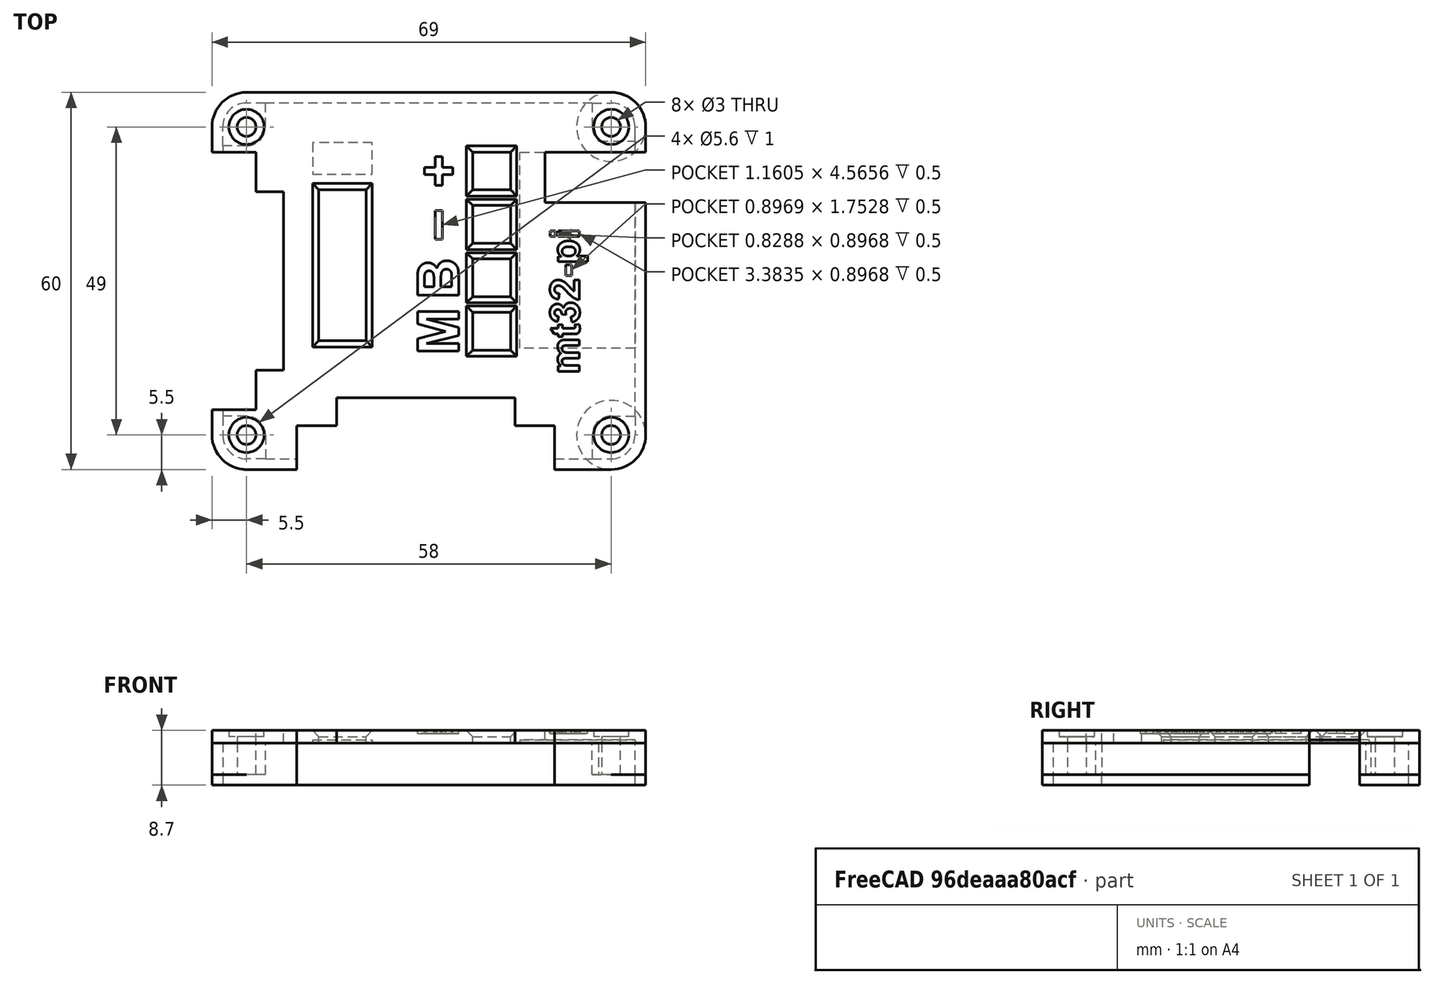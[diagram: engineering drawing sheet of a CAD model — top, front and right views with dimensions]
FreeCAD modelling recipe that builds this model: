
FCSTD DOCUMENT  (FreeCAD 0.21R33668 +26 (Git))
Label: case
License: All rights reserved
LicenseURL: https://en.wikipedia.org/wiki/All_rights_reserved
objects: Sketcher::SketchObject×9, Part::Extrusion×9, Part::Cut×8, Part::Part2DObjectPython×1, Part::Chamfer×1, Part::MultiFuse×1, Mesh::Feature×1
note: 29 computed .brp shape members not serialized (recipe doc carries the construction recipe); baked Part::Feature solids carry a one-line shape summary decoded from their .brp

FEATURE [Sketcher::SketchObject] Sketch001
  FullyConstrained = true
  MapMode = 5
  sketch-geometry (30):
    g0: LineSegment StartX=5.50002 StartY=-5.68372e-08 StartZ=0 EndX=63.5 EndY=-5.68372e-08 EndZ=0
    g1: LineSegment StartX=69 StartY=5.5 StartZ=0 EndX=69 EndY=54.5 EndZ=0
    g2: LineSegment StartX=63.5 StartY=60 StartZ=0 EndX=5.50002 EndY=60 EndZ=0
    g3: LineSegment StartX=8.50002 StartY=1.7 StartZ=0 EndX=60.5 EndY=1.7 EndZ=0
    g4: LineSegment StartX=67.3 StartY=8.5 StartZ=0 EndX=67.3 EndY=51.5 EndZ=0
    g5: LineSegment StartX=60.5 StartY=58.3 StartZ=0 EndX=8.50002 EndY=58.3 EndZ=0
    g6: ArcOfCircle CenterX=63.5 CenterY=54.5 CenterZ=0 NormalX=0 NormalY=0 NormalZ=1 AngleXU=0 Radius=5.5 StartAngle=0 EndAngle=1.5708
    g7: ArcOfCircle CenterX=63.5 CenterY=5.5 CenterZ=0 NormalX=0 NormalY=0 NormalZ=1 AngleXU=0 Radius=5.5 StartAngle=4.71239 EndAngle=6.28319
    g8: ArcOfCircle CenterX=5.50002 CenterY=54.5 CenterZ=0 NormalX=0 NormalY=0 NormalZ=1 AngleXU=0 Radius=5.5 StartAngle=1.5708 EndAngle=3.14159
    g9: Circle CenterX=63.5 CenterY=5.5 CenterZ=0 NormalX=0 NormalY=0 NormalZ=1 AngleXU=0 Radius=1.5
    g10: Circle CenterX=63.5 CenterY=54.5 CenterZ=0 NormalX=0 NormalY=0 NormalZ=1 AngleXU=0 Radius=1.5
    g11: Circle CenterX=5.50002 CenterY=54.5 CenterZ=0 NormalX=0 NormalY=0 NormalZ=1 AngleXU=0 Radius=1.5
    g12: ArcOfCircle CenterX=5.50002 CenterY=54.5 CenterZ=0 NormalX=0 NormalY=0 NormalZ=1 AngleXU=0 Radius=3 StartAngle=4.71239 EndAngle=6.28319
    g13: ArcOfCircle CenterX=63.5 CenterY=54.5 CenterZ=0 NormalX=0 NormalY=0 NormalZ=1 AngleXU=0 Radius=3 StartAngle=3.14159 EndAngle=4.71239
    g14: ArcOfCircle CenterX=63.5 CenterY=5.5 CenterZ=0 NormalX=0 NormalY=0 NormalZ=1 AngleXU=0 Radius=3 StartAngle=1.5708 EndAngle=3.14159
    g15: ArcOfCircle CenterX=5.50002 CenterY=5.5 CenterZ=0 NormalX=0 NormalY=0 NormalZ=1 AngleXU=0 Radius=3 StartAngle=0 EndAngle=1.5708
    g16: LineSegment StartX=8.50002 StartY=54.5 StartZ=0 EndX=8.50002 EndY=58.3 EndZ=0
    g17: LineSegment StartX=5.50002 StartY=51.5 StartZ=0 EndX=1.70002 EndY=51.5 EndZ=0
    g18: LineSegment StartX=1.70002 StartY=51.5 StartZ=0 EndX=1.70002 EndY=8.5 EndZ=0
    g19: LineSegment StartX=5.50002 StartY=8.5 StartZ=0 EndX=1.70002 EndY=8.5 EndZ=0
    g20: LineSegment StartX=8.50002 StartY=5.5 StartZ=0 EndX=8.50002 EndY=1.7 EndZ=0
    g21: Circle CenterX=5.50002 CenterY=5.5 CenterZ=0 NormalX=0 NormalY=0 NormalZ=1 AngleXU=0 Radius=1.5
    g22: LineSegment StartX=63.5 StartY=51.5 StartZ=0 EndX=67.3 EndY=51.5 EndZ=0
    g23: LineSegment StartX=63.5 StartY=8.5 StartZ=0 EndX=67.3 EndY=8.5 EndZ=0
    g24: LineSegment StartX=60.5 StartY=5.5 StartZ=0 EndX=60.5 EndY=1.7 EndZ=0
    g25: LineSegment StartX=60.5 StartY=58.3 StartZ=0 EndX=60.5 EndY=54.5 EndZ=0
    g26: LineSegment StartX=2.09555e-05 StartY=54.5 StartZ=0 EndX=2.09555e-05 EndY=5.5 EndZ=0
    g27: ArcOfCircle CenterX=5.50002 CenterY=5.5 CenterZ=0 NormalX=0 NormalY=0 NormalZ=1 AngleXU=0 Radius=5.5 StartAngle=3.14159 EndAngle=4.71239
    g28: LineSegment StartX=5.50002 StartY=-5.68372e-08 StartZ=0 EndX=0 EndY=0 EndZ=0
    g29: LineSegment StartX=2.09555e-05 StartY=5.5 StartZ=0 EndX=0 EndY=0 EndZ=0
  constraints (72):
    c: Horizontal(g0)
    c: Horizontal(g2)
    c: Vertical(g1)
    c: Horizontal(g3)
    c: Horizontal(g5)
    c: Vertical(g4)
    c: Coincident(g11,g8)
    c: Coincident(g12,g8)
    c: Vertical(g16)
    c: Horizontal(g17)
    c: Tangent(g12,g17) = 1.5708
    c: Tangent(g12,g16) = -1.5708
    c: Coincident(g5,g16)
    c: Coincident(g18,g17)
    c: Vertical(g18)
    c: Horizontal(g19)
    c: Vertical(g20)
    c: Coincident(g18,g19)
    c: Tangent(g15,g19) = -1.5708
    c: Tangent(g15,g20) = 1.5708
    c: Coincident(g3,g20)
    c: Distance(g0,g2) = 60
    c: Horizontal(g22)
    c: Horizontal(g23)
    c: Vertical(g24)
    c: Coincident(g3,g24)
    c: Coincident(g4,g23)
    c: Tangent(g14,g24) = -1.5708
    c: Tangent(g14,g23) = 1.5708
    c: Tangent(g13,g22) = -1.5708
    c: Coincident(g4,g22)
    c: Coincident(g25,g5)
    c: Vertical(g25)
    c: Equal(g11,g10)
    c: Equal(g10,g9)
    c: Equal(g9,g21)
    c: Equal(g13,g12)
    c: Equal(g12,g15)
    c: Equal(g15,g14)
    c: Coincident(g6,g13)
    c: Coincident(g6,g10)
    c: Tangent(g25,g13) = -1.5708
    c: Coincident(g14,g7)
    c: Coincident(g14,g9)
    c: Tangent(g2,g8) = -1.5708
    c: Tangent(g2,g6) = -1.5708
    c: Tangent(g1,g6) = -1.5708
    c: Tangent(g1,g7) = -1.5708
    c: Tangent(g0,g7) = -1.5708
    c: Equal(g16,g19)
    c: Equal(g19,g24)
    c: Equal(g24,g23)
    c: Diameter(g11) = 3
    c: Distance(g5,g2) = 1.7
    c: Radius(g12) = 3
    c: Vertical(g26)
    c: Coincident(g27,g15)
    c: Tangent(g27,g26) = -1.5708
    c: Tangent(g27,g0) = -1.5708
    c: Coincident(g28,g0)
    c: Coincident(g28,g-1)
    c: Tangent(g28,g27)
    c: Coincident(g29,g26)
    c: Coincident(g29,g28)
    c: Tangent(g29,g27)
    c: Tangent(g26,g8) = -1.5708
    c: Equal(g8,g27)
    c: Equal(g27,g7)
    c: Equal(g7,g6)
    c: Coincident(g21,g15)
    c: Distance(g8,g1) = 69
    c: Distance(g8,g26) = 5.5
FEATURE [Part::Extrusion] Extrude
  Base = -> Sketch001
  Dir = (0,0,1)
  DirMode = 2
  FaceMakerClass = Part::FaceMakerBullseye
  LengthFwd = 5
  LengthRev = 0
  Solid = true
  Symmetric = false
FEATURE [Sketcher::SketchObject] Sketch002
  FullyConstrained = true
  MapMode = 5
  expr: Constraints[21] = Sketch001.Constraints[21]
  expr: Constraints[52] = Sketch001.Constraints[52]
  expr: Constraints[53] = Sketch001.Constraints[53]
  expr: Constraints[54] = Sketch001.Constraints[54]
  expr: Constraints[70] = Sketch001.Constraints[70]
  expr: Constraints[71] = Sketch001.Constraints[71]
  sketch-geometry (42):
    g0: LineSegment StartX=5.5 StartY=-9.28724e-08 StartZ=0 EndX=63.5 EndY=-9.28724e-08 EndZ=0
    g1: LineSegment StartX=69 StartY=5.5 StartZ=0 EndX=69 EndY=54.5 EndZ=0
    g2: LineSegment StartX=63.5 StartY=60 StartZ=0 EndX=5.5 EndY=60 EndZ=0
    g3: LineSegment StartX=8.5 StartY=1.7 StartZ=0 EndX=60.5 EndY=1.7 EndZ=0
    g4: LineSegment StartX=67.3 StartY=8.5 StartZ=0 EndX=67.3 EndY=51.5 EndZ=0
    g5: LineSegment StartX=60.5 StartY=58.3 StartZ=0 EndX=8.5 EndY=58.3 EndZ=0
    g6: ArcOfCircle CenterX=63.5 CenterY=54.5 CenterZ=0 NormalX=0 NormalY=0 NormalZ=1 AngleXU=0 Radius=5.5 StartAngle=0 EndAngle=1.5708
    g7: ArcOfCircle CenterX=63.5 CenterY=5.5 CenterZ=0 NormalX=0 NormalY=0 NormalZ=1 AngleXU=0 Radius=5.5 StartAngle=4.71239 EndAngle=6.28319
    g8: ArcOfCircle CenterX=5.5 CenterY=54.5 CenterZ=0 NormalX=0 NormalY=0 NormalZ=1 AngleXU=0 Radius=5.5 StartAngle=1.5708 EndAngle=3.14159
    g9: Circle CenterX=63.5 CenterY=5.5 CenterZ=0 NormalX=0 NormalY=0 NormalZ=1 AngleXU=0 Radius=1.5
    g10: Circle CenterX=63.5 CenterY=54.5 CenterZ=0 NormalX=0 NormalY=0 NormalZ=1 AngleXU=0 Radius=1.5
    g11: Circle CenterX=5.5 CenterY=54.5 CenterZ=0 NormalX=0 NormalY=0 NormalZ=1 AngleXU=0 Radius=1.5
    g12: ArcOfCircle CenterX=5.5 CenterY=54.5 CenterZ=0 NormalX=0 NormalY=0 NormalZ=1 AngleXU=0 Radius=3 StartAngle=4.71239 EndAngle=6.28319
    g13: ArcOfCircle CenterX=63.5 CenterY=54.5 CenterZ=0 NormalX=0 NormalY=0 NormalZ=1 AngleXU=0 Radius=3 StartAngle=3.14159 EndAngle=4.71239
    g14: ArcOfCircle CenterX=63.5 CenterY=5.5 CenterZ=0 NormalX=0 NormalY=0 NormalZ=1 AngleXU=0 Radius=3 StartAngle=1.5708 EndAngle=3.14159
    g15: ArcOfCircle CenterX=5.5 CenterY=5.5 CenterZ=0 NormalX=0 NormalY=0 NormalZ=1 AngleXU=0 Radius=3 StartAngle=0 EndAngle=1.5708
    g16: LineSegment StartX=8.5 StartY=54.5 StartZ=0 EndX=8.5 EndY=58.3 EndZ=0
    g17: LineSegment StartX=5.5 StartY=51.5 StartZ=0 EndX=1.7 EndY=51.5 EndZ=0
    g18: LineSegment StartX=1.7 StartY=51.5 StartZ=0 EndX=1.7 EndY=8.5 EndZ=0
    g19: LineSegment StartX=5.5 StartY=8.5 StartZ=0 EndX=1.7 EndY=8.5 EndZ=0
    g20: LineSegment StartX=8.5 StartY=5.5 StartZ=0 EndX=8.5 EndY=1.7 EndZ=0
    g21: Circle CenterX=5.5 CenterY=5.5 CenterZ=0 NormalX=0 NormalY=0 NormalZ=1 AngleXU=0 Radius=1.5
    g22: LineSegment StartX=63.5 StartY=51.5 StartZ=0 EndX=67.3 EndY=51.5 EndZ=0
    g23: LineSegment StartX=63.5 StartY=8.5 StartZ=0 EndX=67.3 EndY=8.5 EndZ=0
    g24: LineSegment StartX=60.5 StartY=5.5 StartZ=0 EndX=60.5 EndY=1.7 EndZ=0
    g25: LineSegment StartX=60.5 StartY=58.3 StartZ=0 EndX=60.5 EndY=54.5 EndZ=0
    g26: LineSegment StartX=2.40654e-07 StartY=54.5 StartZ=0 EndX=2.40654e-07 EndY=5.5 EndZ=0
    g27: ArcOfCircle CenterX=5.5 CenterY=5.5 CenterZ=0 NormalX=0 NormalY=0 NormalZ=1 AngleXU=0 Radius=5.5 StartAngle=3.14159 EndAngle=4.71239
    g28: LineSegment StartX=5.5 StartY=-9.28724e-08 StartZ=0 EndX=0 EndY=0 EndZ=0
    g29: LineSegment StartX=2.40654e-07 StartY=5.5 StartZ=0 EndX=0 EndY=0 EndZ=0
    g30: LineSegment StartX=1.7 StartY=51.5 StartZ=0 EndX=1.7 EndY=54.5 EndZ=0
    g31: LineSegment StartX=8.5 StartY=58.3 StartZ=0 EndX=5.5 EndY=58.3 EndZ=0
    g32: ArcOfCircle CenterX=5.5 CenterY=54.5 CenterZ=0 NormalX=0 NormalY=0 NormalZ=1 AngleXU=0 Radius=3.8 StartAngle=1.5708 EndAngle=3.14159
    g33: LineSegment StartX=60.5 StartY=58.3 StartZ=0 EndX=63.5 EndY=58.3 EndZ=0
    g34: LineSegment StartX=67.3 StartY=51.5 StartZ=0 EndX=67.3 EndY=54.5 EndZ=0
    g35: LineSegment StartX=67.3 StartY=8.5 StartZ=0 EndX=67.3 EndY=5.5 EndZ=0
    g36: LineSegment StartX=60.5 StartY=1.7 StartZ=0 EndX=63.5 EndY=1.7 EndZ=0
    g37: LineSegment StartX=8.5 StartY=1.7 StartZ=0 EndX=5.5 EndY=1.7 EndZ=0
    g38: LineSegment StartX=1.7 StartY=8.5 StartZ=0 EndX=1.7 EndY=5.5 EndZ=0
    g39: ArcOfCircle CenterX=5.5 CenterY=5.5 CenterZ=0 NormalX=0 NormalY=0 NormalZ=1 AngleXU=0 Radius=3.8 StartAngle=3.14159 EndAngle=4.71239
    g40: ArcOfCircle CenterX=63.5 CenterY=5.5 CenterZ=0 NormalX=0 NormalY=0 NormalZ=1 AngleXU=0 Radius=3.8 StartAngle=4.71239 EndAngle=6.28319
    g41: ArcOfCircle CenterX=63.5 CenterY=54.5 CenterZ=0 NormalX=0 NormalY=0 NormalZ=1 AngleXU=0 Radius=3.8 StartAngle=6e-16 EndAngle=1.5708
  constraints (100):
    c: Horizontal(g0)
    c: Horizontal(g2)
    c: Vertical(g1)
    c: Horizontal(g3)
    c: Horizontal(g5)
    c: Vertical(g4)
    c: Coincident(g11,g8)
    c: Coincident(g12,g8)
    c: Vertical(g16)
    c: Horizontal(g17)
    c: Tangent(g12,g17) = 1.5708
    c: Tangent(g12,g16) = -1.5708
    c: Coincident(g5,g16)
    c: Coincident(g18,g17)
    c: Vertical(g18)
    c: Horizontal(g19)
    c: Vertical(g20)
    c: Coincident(g18,g19)
    c: Tangent(g15,g19) = -1.5708
    c: Tangent(g15,g20) = 1.5708
    c: Coincident(g3,g20)
    c: Distance(g0,g2) = 60
    c: Horizontal(g22)
    c: Horizontal(g23)
    c: Vertical(g24)
    c: Coincident(g3,g24)
    c: Coincident(g4,g23)
    c: Tangent(g14,g24) = -1.5708
    c: Tangent(g14,g23) = 1.5708
    c: Tangent(g13,g22) = -1.5708
    c: Coincident(g4,g22)
    c: Coincident(g25,g5)
    c: Vertical(g25)
    c: Equal(g11,g10)
    c: Equal(g10,g9)
    c: Equal(g9,g21)
    c: Equal(g13,g12)
    c: Equal(g12,g15)
    c: Equal(g15,g14)
    c: Coincident(g6,g13)
    c: Coincident(g6,g10)
    c: Tangent(g25,g13) = -1.5708
    c: Coincident(g14,g7)
    c: Coincident(g14,g9)
    c: Tangent(g2,g8) = -1.5708
    c: Tangent(g2,g6) = -1.5708
    c: Tangent(g1,g6) = -1.5708
    c: Tangent(g1,g7) = -1.5708
    c: Tangent(g0,g7) = -1.5708
    c: Equal(g16,g19)
    c: Equal(g19,g24)
    c: Equal(g24,g23)
    c: Diameter(g11) = 3
    c: Distance(g5,g2) = 1.7
    c: Radius(g12) = 3
    c: Vertical(g26)
    c: Coincident(g27,g15)
    c: Tangent(g27,g26) = -1.5708
    c: Tangent(g27,g0) = -1.5708
    c: Coincident(g28,g0)
    c: Coincident(g28,g-1)
    c: Tangent(g28,g27)
    c: Coincident(g29,g26)
    c: Coincident(g29,g28)
    c: Tangent(g29,g27)
    c: Tangent(g26,g8) = -1.5708
    c: Equal(g8,g27)
    c: Equal(g27,g7)
    c: Equal(g7,g6)
    c: Coincident(g21,g15)
    c: Distance(g8,g1) = 69
    c: Distance(g8,g26) = 5.5
    c: Coincident(g30,g17)
    c: Vertical(g30)
    c: Coincident(g31,g5)
    c: Horizontal(g31)
    c: Coincident(g32,g8)
    c: Coincident(g32,g31)
    c: Tangent(g32,g30) = 1.5708
    c: Coincident(g33,g5)
    c: Horizontal(g33)
    c: Coincident(g34,g4)
    c: Vertical(g34)
    c: Coincident(g35,g4)
    c: Vertical(g35)
    c: Coincident(g36,g3)
    c: Horizontal(g36)
    c: Coincident(g37,g3)
    c: Horizontal(g37)
    c: Coincident(g38,g18)
    c: Vertical(g38)
    c: Coincident(g39,g15)
    c: Coincident(g39,g38)
    c: Coincident(g40,g7)
    c: Coincident(g40,g36)
    c: Coincident(g41,g6)
    c: Coincident(g41,g33)
    c: Tangent(g41,g34) = -1.5708
    c: Tangent(g40,g35) = 1.5708
    c: Tangent(g39,g37) = 1.5708
FEATURE [Sketcher::SketchObject] Sketch003
  FullyConstrained = true
  MapMode = 5
  Placement = pos=(0,0,5) rot=(0,0,1;0rad)
  Support = -> [Extrude]
  expr: Constraints[109] = Sketch001.Constraints[21]
  expr: Constraints[140] = Sketch001.Constraints[52]
  expr: Constraints[141] = Sketch001.Constraints[53]
  expr: Constraints[142] = Sketch001.Constraints[54]
  expr: Constraints[158] = Sketch001.Constraints[70]
  expr: Constraints[159] = Sketch001.Constraints[71]
  sketch-geometry (64):
    g0: LineSegment StartX=17 StartY=44.5 StartZ=0 EndX=24.5 EndY=44.5 EndZ=0
    g1: LineSegment StartX=24.5 StartY=44.5 StartZ=0 EndX=24.5 EndY=20.5 EndZ=0
    g2: LineSegment StartX=24.5 StartY=20.5 StartZ=0 EndX=17 EndY=20.5 EndZ=0
    g3: LineSegment StartX=17 StartY=20.5 StartZ=0 EndX=17 EndY=44.5 EndZ=0
    g4: LineSegment StartX=41.5 StartY=50.5 StartZ=0 EndX=47.5 EndY=50.5 EndZ=0
    g5: LineSegment StartX=47.5 StartY=50.5 StartZ=0 EndX=47.5 EndY=44.5 EndZ=0
    g6: LineSegment StartX=47.5 StartY=44.5 StartZ=0 EndX=41.5 EndY=44.5 EndZ=0
    g7: LineSegment StartX=41.5 StartY=44.5 StartZ=0 EndX=41.5 EndY=50.5 EndZ=0
    g8: LineSegment StartX=41.5 StartY=42 StartZ=0 EndX=47.5 EndY=42 EndZ=0
    g9: LineSegment StartX=47.5 StartY=42 StartZ=0 EndX=47.5 EndY=36 EndZ=0
    g10: LineSegment StartX=47.5 StartY=36 StartZ=0 EndX=41.5 EndY=36 EndZ=0
    g11: LineSegment StartX=41.5 StartY=36 StartZ=0 EndX=41.5 EndY=42 EndZ=0
    g12: LineSegment StartX=41.5 StartY=33.5 StartZ=0 EndX=47.5 EndY=33.5 EndZ=0
    g13: LineSegment StartX=47.5 StartY=33.5 StartZ=0 EndX=47.5 EndY=27.5 EndZ=0
    g14: LineSegment StartX=47.5 StartY=27.5 StartZ=0 EndX=41.5 EndY=27.5 EndZ=0
    g15: LineSegment StartX=41.5 StartY=27.5 StartZ=0 EndX=41.5 EndY=33.5 EndZ=0
    g16: LineSegment StartX=41.5 StartY=25 StartZ=0 EndX=47.5 EndY=25 EndZ=0
    g17: LineSegment StartX=47.5 StartY=25 StartZ=0 EndX=47.5 EndY=19 EndZ=0
    g18: LineSegment StartX=47.5 StartY=19 StartZ=0 EndX=41.5 EndY=19 EndZ=0
    g19: LineSegment StartX=41.5 StartY=19 StartZ=0 EndX=41.5 EndY=25 EndZ=0
    g20: LineSegment StartX=41.5 StartY=44.5 StartZ=0 EndX=41.5 EndY=42 EndZ=0
    g21: LineSegment StartX=41.5 StartY=36 StartZ=0 EndX=41.5 EndY=33.5 EndZ=0
    g22: LineSegment StartX=41.5 StartY=27.5 StartZ=0 EndX=41.5 EndY=25 EndZ=0
    g23: LineSegment StartX=47.5 StartY=25 StartZ=0 EndX=47.5 EndY=27.5 EndZ=0
    g24: LineSegment StartX=47.5 StartY=33.5 StartZ=0 EndX=47.5 EndY=36 EndZ=0
    g25: LineSegment StartX=47.5 StartY=42 StartZ=0 EndX=47.5 EndY=44.5 EndZ=0
    g26: LineSegment StartX=61.73 StartY=18.27 StartZ=0 EndX=65.28 EndY=18.27 EndZ=0
    g27: LineSegment StartX=65.28 StartY=18.27 StartZ=0 EndX=65.28 EndY=9.62 EndZ=0
    g28: LineSegment StartX=65.28 StartY=9.62 StartZ=0 EndX=61.73 EndY=9.62 EndZ=0
    g29: LineSegment StartX=61.73 StartY=9.62 StartZ=0 EndX=61.73 EndY=18.27 EndZ=0
    g30: LineSegment StartX=55.5 StartY=11.85 StartZ=0 EndX=59.05 EndY=11.85 EndZ=0
    g31: LineSegment StartX=59.05 StartY=11.85 StartZ=0 EndX=59.05 EndY=3.2 EndZ=0
    g32: LineSegment StartX=59.05 StartY=3.2 StartZ=0 EndX=55.5 EndY=3.2 EndZ=0
    g33: LineSegment StartX=55.5 StartY=3.2 StartZ=0 EndX=55.5 EndY=11.85 EndZ=0
    g34: LineSegment StartX=5.5 StartY=2.71047e-06 StartZ=0 EndX=63.5 EndY=2.71047e-06 EndZ=0
    g35: LineSegment StartX=69 StartY=5.5 StartZ=0 EndX=69 EndY=54.5 EndZ=0
    g36: LineSegment StartX=63.5 StartY=60 StartZ=0 EndX=5.5 EndY=60 EndZ=0
    g37: LineSegment StartX=8.5 StartY=1.7 StartZ=0 EndX=60.5 EndY=1.7 EndZ=0
    g38: LineSegment StartX=67.3 StartY=8.5 StartZ=0 EndX=67.3 EndY=51.5 EndZ=0
    g39: LineSegment StartX=60.5 StartY=58.3 StartZ=0 EndX=8.5 EndY=58.3 EndZ=0
    g40: ArcOfCircle CenterX=63.5 CenterY=54.5 CenterZ=0 NormalX=0 NormalY=0 NormalZ=1 AngleXU=0 Radius=5.5 StartAngle=4e-16 EndAngle=1.5708
    g41: ArcOfCircle CenterX=63.5 CenterY=5.5 CenterZ=0 NormalX=0 NormalY=0 NormalZ=1 AngleXU=0 Radius=5.5 StartAngle=4.71239 EndAngle=6.28319
    g42: ArcOfCircle CenterX=5.5 CenterY=54.5 CenterZ=0 NormalX=0 NormalY=0 NormalZ=1 AngleXU=0 Radius=5.5 StartAngle=1.5708 EndAngle=3.14159
    g43: Circle CenterX=63.5 CenterY=5.5 CenterZ=0 NormalX=0 NormalY=0 NormalZ=1 AngleXU=0 Radius=1.5
    g44: Circle CenterX=63.5 CenterY=54.5 CenterZ=0 NormalX=0 NormalY=0 NormalZ=1 AngleXU=0 Radius=1.5
    g45: Circle CenterX=5.5 CenterY=54.5 CenterZ=0 NormalX=0 NormalY=0 NormalZ=1 AngleXU=0 Radius=1.5
    g46: ArcOfCircle CenterX=5.5 CenterY=54.5 CenterZ=0 NormalX=0 NormalY=0 NormalZ=1 AngleXU=0 Radius=3 StartAngle=4.71239 EndAngle=6.28319
    g47: ArcOfCircle CenterX=63.5 CenterY=54.5 CenterZ=0 NormalX=0 NormalY=0 NormalZ=1 AngleXU=0 Radius=3 StartAngle=3.14159 EndAngle=4.71239
    g48: ArcOfCircle CenterX=63.5 CenterY=5.5 CenterZ=0 NormalX=0 NormalY=0 NormalZ=1 AngleXU=0 Radius=3 StartAngle=1.5708 EndAngle=3.14159
    g49: ArcOfCircle CenterX=5.5 CenterY=5.5 CenterZ=0 NormalX=0 NormalY=0 NormalZ=1 AngleXU=0 Radius=3 StartAngle=0 EndAngle=1.5708
    g50: LineSegment StartX=8.5 StartY=54.5 StartZ=0 EndX=8.5 EndY=58.3 EndZ=0
    g51: LineSegment StartX=5.5 StartY=51.5 StartZ=0 EndX=1.7 EndY=51.5 EndZ=0
    g52: LineSegment StartX=1.7 StartY=51.5 StartZ=0 EndX=1.7 EndY=8.5 EndZ=0
    g53: LineSegment StartX=5.5 StartY=8.5 StartZ=0 EndX=1.7 EndY=8.5 EndZ=0
    g54: LineSegment StartX=8.5 StartY=5.5 StartZ=0 EndX=8.5 EndY=1.7 EndZ=0
    g55: Circle CenterX=5.5 CenterY=5.5 CenterZ=0 NormalX=0 NormalY=0 NormalZ=1 AngleXU=0 Radius=1.5
    g56: LineSegment StartX=63.5 StartY=51.5 StartZ=0 EndX=67.3 EndY=51.5 EndZ=0
    g57: LineSegment StartX=63.5 StartY=8.5 StartZ=0 EndX=67.3 EndY=8.5 EndZ=0
    g58: LineSegment StartX=60.5 StartY=5.5 StartZ=0 EndX=60.5 EndY=1.7 EndZ=0
    g59: LineSegment StartX=60.5 StartY=58.3 StartZ=0 EndX=60.5 EndY=54.5 EndZ=0
    g60: LineSegment StartX=2.53122e-07 StartY=54.5 StartZ=0 EndX=2.53122e-07 EndY=5.5 EndZ=0
    g61: ArcOfCircle CenterX=5.5 CenterY=5.5 CenterZ=0 NormalX=0 NormalY=0 NormalZ=1 AngleXU=0 Radius=5.5 StartAngle=3.14159 EndAngle=4.71239
    g62: LineSegment StartX=5.5 StartY=2.71047e-06 StartZ=0 EndX=0 EndY=0 EndZ=0
    g63: LineSegment StartX=2.53122e-07 StartY=5.5 StartZ=0 EndX=0 EndY=0 EndZ=0
  constraints (168):
    c: Coincident(g0,g1)
    c: Coincident(g1,g2)
    c: Coincident(g2,g3)
    c: Coincident(g3,g0)
    c: Horizontal(g0)
    c: Horizontal(g2)
    c: Vertical(g1)
    c: Vertical(g3)
    c: Coincident(g4,g5)
    c: Coincident(g5,g6)
    c: Coincident(g6,g7)
    c: Coincident(g7,g4)
    c: Horizontal(g4)
    c: Horizontal(g6)
    c: Vertical(g5)
    c: Vertical(g7)
    c: Coincident(g8,g9)
    c: Coincident(g9,g10)
    c: Coincident(g10,g11)
    c: Coincident(g11,g8)
    c: Horizontal(g8)
    c: Horizontal(g10)
    c: Vertical(g9)
    c: Vertical(g11)
    c: Coincident(g12,g13)
    c: Coincident(g13,g14)
    c: Coincident(g14,g15)
    c: Coincident(g15,g12)
    c: Horizontal(g12)
    c: Horizontal(g14)
    c: Vertical(g13)
    c: Vertical(g15)
    c: Coincident(g16,g17)
    c: Coincident(g17,g18)
    c: Coincident(g18,g19)
    c: Coincident(g19,g16)
    c: Horizontal(g16)
    c: Horizontal(g18)
    c: Vertical(g17)
    c: Vertical(g19)
    c: Coincident(g20,g6)
    c: Coincident(g20,g8)
    c: Coincident(g21,g10)
    c: Coincident(g21,g12)
    c: Coincident(g22,g14)
    c: Coincident(g22,g16)
    c: Coincident(g23,g16)
    c: Coincident(g23,g13)
    c: Coincident(g24,g12)
    c: Coincident(g24,g9)
    c: Coincident(g25,g8)
    c: Coincident(g25,g5)
    c: Vertical(g20)
    c: Vertical(g25)
    c: Vertical(g21)
    c: Vertical(g24)
    c: Vertical(g23)
    c: Vertical(g22)
    c: Equal(g15,g11)
    c: Equal(g11,g7)
    c: Equal(g7,g19)
    c: Equal(g20,g21)
    c: Equal(g21,g22)
    c: Distance(g4) = 6
    c: Distance(g5) = 6
    c: DistanceY(g8,g4) = 8.5
    c: Distance(g3) = 24
    c: Distance(g0) = 7.5
    c: Coincident(g26,g27)
    c: Coincident(g27,g28)
    c: Coincident(g28,g29)
    c: Coincident(g29,g26)
    c: Horizontal(g26)
    c: Horizontal(g28)
    c: Vertical(g27)
    c: Vertical(g29)
    c: Coincident(g30,g31)
    c: Coincident(g31,g32)
    c: Coincident(g32,g33)
    c: Coincident(g33,g30)
    c: Horizontal(g30)
    c: Horizontal(g32)
    c: Vertical(g31)
    c: Vertical(g33)
    c: Equal(g33,g29)
    c: Equal(g30,g26)
    c: Distance(g33) = 8.65
    c: Distance(g30) = 3.55
    c: Horizontal(g34)
    c: Horizontal(g36)
    c: Vertical(g35)
    c: Horizontal(g37)
    c: Horizontal(g39)
    c: Vertical(g38)
    c: Coincident(g45,g42)
    c: Coincident(g46,g42)
    c: Vertical(g50)
    c: Horizontal(g51)
    c: Tangent(g46,g51) = 1.5708
    c: Tangent(g46,g50) = -1.5708
    c: Coincident(g39,g50)
    c: Coincident(g52,g51)
    c: Vertical(g52)
    c: Horizontal(g53)
    c: Vertical(g54)
    c: Coincident(g52,g53)
    c: Tangent(g49,g53) = -1.5708
    c: Tangent(g49,g54) = 1.5708
    c: Coincident(g37,g54)
    c: Distance(g34,g36) = 60
    c: Horizontal(g56)
    c: Horizontal(g57)
    c: Vertical(g58)
    c: Coincident(g37,g58)
    c: Coincident(g38,g57)
    c: Tangent(g48,g58) = -1.5708
    c: Tangent(g48,g57) = 1.5708
    c: Tangent(g47,g56) = -1.5708
    c: Coincident(g38,g56)
    c: Coincident(g59,g39)
    c: Vertical(g59)
    c: Equal(g45,g44)
    c: Equal(g44,g43)
    c: Equal(g43,g55)
    c: Equal(g47,g46)
    c: Equal(g46,g49)
    c: Equal(g49,g48)
    c: Coincident(g40,g47)
    c: Coincident(g40,g44)
    c: Tangent(g59,g47) = -1.5708
    c: Coincident(g48,g41)
    c: Coincident(g48,g43)
    c: Tangent(g36,g42) = -1.5708
    c: Tangent(g36,g40) = -1.5708
    c: Tangent(g35,g40) = -1.5708
    c: Tangent(g35,g41) = -1.5708
    c: Tangent(g34,g41) = -1.5708
    c: Equal(g50,g53)
    c: Equal(g53,g58)
    c: Equal(g58,g57)
    c: Diameter(g45) = 3
    c: Distance(g39,g36) = 1.7
    c: Radius(g46) = 3
    c: Vertical(g60)
    c: Coincident(g61,g49)
    c: Tangent(g61,g60) = -1.5708
    c: Tangent(g61,g34) = -1.5708
    c: Coincident(g62,g34)
    c: Coincident(g62,g-1)
    c: Tangent(g62,g61)
    c: Coincident(g63,g60)
    c: Coincident(g63,g62)
    c: Tangent(g63,g61)
    c: Tangent(g60,g42) = -1.5708
    c: Equal(g42,g61)
    c: Equal(g61,g41)
    c: Equal(g41,g40)
    c: Coincident(g55,g49)
    c: Distance(g42,g35) = 69
    c: Distance(g42,g60) = 5.5
    c: Distance(g4,g36) = 9.5
    c: Distance(g4,g35) = 21.5
    c: Distance(g42,g3) = 11.5
    c: Distance(g42,g0) = 10
    c: Distance(g41,g31) = 4.45
    c: Distance(g41,g32) = 2.3
    c: Distance(g41,g27) = 1.78
    c: Distance(g41,g28) = 4.12
FEATURE [Part::Extrusion] Extrude001
  Base = -> Sketch002
  Dir = (0,0,1)
  DirMode = 2
  FaceMakerClass = Part::FaceMakerBullseye
  LengthFwd = 0
  LengthRev = 1.7
  Solid = true
  Symmetric = false
FEATURE [Part::Extrusion] Extrude002
  Base = -> Sketch003
  Dir = (0,0,1)
  DirMode = 2
  FaceMakerClass = Part::FaceMakerBullseye
  LengthFwd = 2
  LengthRev = 0
  Solid = true
  Symmetric = false
FEATURE [Sketcher::SketchObject] Sketch
  FullyConstrained = true
  MapMode = 2
  Support = -> [Sketch001]
  sketch-geometry (24):
    g0: LineSegment StartX=0 StartY=0 StartZ=0 EndX=69 EndY=0 EndZ=0
    g1: LineSegment StartX=69 StartY=0 StartZ=0 EndX=69 EndY=60 EndZ=0
    g2: LineSegment StartX=69 StartY=60 StartZ=0 EndX=0 EndY=60 EndZ=0
    g3: LineSegment StartX=0 StartY=60 StartZ=0 EndX=0 EndY=0 EndZ=0
    g4: LineSegment StartX=0 StartY=9.5 StartZ=0 EndX=0 EndY=50.5 EndZ=0
    g5: LineSegment StartX=13.5 StartY=0 StartZ=0 EndX=54.5 EndY=0 EndZ=0
    g6: LineSegment StartX=54.5 StartY=0 StartZ=0 EndX=54.5 EndY=7 EndZ=0
    g7: LineSegment StartX=48.2 StartY=11.4 StartZ=0 EndX=19.8 EndY=11.4 EndZ=0
    g8: LineSegment StartX=71 StartY=50.5 StartZ=0 EndX=53 EndY=50.5 EndZ=0
    g9: LineSegment StartX=53 StartY=50.5 StartZ=0 EndX=53 EndY=42.5 EndZ=0
    g10: LineSegment StartX=53 StartY=42.5 StartZ=0 EndX=71 EndY=42.5 EndZ=0
    g11: LineSegment StartX=7 StartY=9.5 StartZ=0 EndX=7 EndY=15.8 EndZ=0
    g12: LineSegment StartX=7 StartY=15.8 StartZ=0 EndX=11.4 EndY=15.8 EndZ=0
    g13: LineSegment StartX=7 StartY=9.5 StartZ=0 EndX=0 EndY=9.5 EndZ=0
    g14: LineSegment StartX=0 StartY=50.5 StartZ=0 EndX=7 EndY=50.5 EndZ=0
    g15: LineSegment StartX=7 StartY=50.5 StartZ=0 EndX=7 EndY=44.2 EndZ=0
    g16: LineSegment StartX=7 StartY=44.2 StartZ=0 EndX=11.4 EndY=44.2 EndZ=0
    g17: LineSegment StartX=11.4 StartY=44.2 StartZ=0 EndX=11.4 EndY=15.8 EndZ=0
    g18: LineSegment StartX=13.5 StartY=7 StartZ=0 EndX=19.8 EndY=7 EndZ=0
    g19: LineSegment StartX=19.8 StartY=11.4 StartZ=0 EndX=19.8 EndY=7 EndZ=0
    g20: LineSegment StartX=48.2 StartY=11.4 StartZ=0 EndX=48.2 EndY=7 EndZ=0
    g21: LineSegment StartX=54.5 StartY=7 StartZ=0 EndX=48.2 EndY=7 EndZ=0
    g22: LineSegment StartX=71 StartY=50.5 StartZ=0 EndX=71 EndY=42.5 EndZ=0
    g23: LineSegment StartX=13.5 StartY=7 StartZ=0 EndX=13.5 EndY=0 EndZ=0
  constraints (71):
    c: Coincident(g0,g1)
    c: Coincident(g1,g2)
    c: Coincident(g2,g3)
    c: Coincident(g3,g0)
    c: Horizontal(g0)
    c: Horizontal(g2)
    c: Vertical(g1)
    c: Vertical(g3)
    c: Coincident(g0,g-1)
    c: Distance(g2) = 69
    c: Distance(g1) = 60
    c: Vertical(g4)
    c: PointOnObject(g4,g3)
    c: Coincident(g5,g6)
    c: Horizontal(g5)
    c: Horizontal(g7)
    c: Vertical(g6)
    c: PointOnObject(g5,g0)
    c: Coincident(g8,g9)
    c: Coincident(g9,g10)
    c: Horizontal(g8)
    c: Horizontal(g10)
    c: Vertical(g9)
    c: Distance(g8,g2) = 9.5
    c: Distance(g8,g1) = 16
    c: Distance(g5,g3) = 13.5
    c: Vertical(g11)
    c: Coincident(g12,g11)
    c: Horizontal(g12)
    c: Coincident(g13,g11)
    c: Coincident(g13,g4)
    c: Horizontal(g13)
    c: Distance(g11,g0) = 9.5
    c: Distance(g12,g4) = 11.4
    c: Distance(g4,g2) = 9.5
    c: Coincident(g14,g4)
    c: Horizontal(g14)
    c: Coincident(g15,g14)
    c: Vertical(g15)
    c: Coincident(g16,g15)
    c: Horizontal(g16)
    c: Coincident(g17,g16)
    c: Coincident(g17,g12)
    c: Vertical(g17)
    c: Distance(g15,g4) = 7
    c: Distance(g15,g14) = 6.3
    c: Horizontal(g18)
    c: Coincident(g19,g18)
    c: Vertical(g19)
    c: Vertical(g20)
    c: Coincident(g21,g20)
    c: Horizontal(g21)
    c: Coincident(g7,g19)
    c: Coincident(g7,g20)
    c: Coincident(g6,g21)
    c: Coincident(g22,g8)
    c: Coincident(g22,g10)
    c: Vertical(g22)
    c: Distance(g8,g1) = 2
    c: Distance(g8,g10) = 8
    c: Equal(g15,g11)
    c: Equal(g11,g18)
    c: Equal(g18,g21)
    c: Coincident(g23,g18)
    c: Coincident(g23,g5)
    c: Vertical(g23)
    c: Equal(g12,g16)
    c: Equal(g16,g19)
    c: Equal(g19,g20)
    c: Equal(g6,g13)
    c: Equal(g5,g4)
FEATURE [Part::Extrusion] Extrude003
  Base = -> Sketch
  Dir = (0,0,1)
  DirMode = 2
  FaceMakerClass = Part::FaceMakerBullseye
  LengthFwd = 20
  LengthRev = 20
  Solid = true
  Symmetric = false
FEATURE [Part::Cut] Cut
  Base = -> Extrude
  Tool = -> Extrude003
FEATURE [Part::Cut] Cut001
  Base = -> Extrude001
  Tool = -> Extrude003
FEATURE [Part::Cut] Cut002
  Base = -> Extrude002
  Tool = -> Extrude003
FEATURE [Sketcher::SketchObject] Sketch004
  FullyConstrained = true
  MapMode = 5
  expr: Constraints[21] = Sketch001.Constraints[21]
  expr: Constraints[52] = Sketch001.Constraints[52]
  expr: Constraints[53] = Sketch001.Constraints[53]
  expr: Constraints[54] = Sketch001.Constraints[54]
  expr: Constraints[70] = Sketch001.Constraints[70]
  expr: Constraints[71] = Sketch001.Constraints[71]
  sketch-geometry (30):
    g0: LineSegment StartX=5.50002 StartY=-5.68372e-08 StartZ=0 EndX=63.5 EndY=-5.68372e-08 EndZ=0
    g1: LineSegment StartX=69 StartY=5.5 StartZ=0 EndX=69 EndY=54.5 EndZ=0
    g2: LineSegment StartX=63.5 StartY=60 StartZ=0 EndX=5.50002 EndY=60 EndZ=0
    g3: LineSegment StartX=8.50002 StartY=1.7 StartZ=0 EndX=60.5 EndY=1.7 EndZ=0
    g4: LineSegment StartX=67.3 StartY=8.5 StartZ=0 EndX=67.3 EndY=51.5 EndZ=0
    g5: LineSegment StartX=60.5 StartY=58.3 StartZ=0 EndX=8.50002 EndY=58.3 EndZ=0
    g6: ArcOfCircle CenterX=63.5 CenterY=54.5 CenterZ=0 NormalX=0 NormalY=0 NormalZ=1 AngleXU=0 Radius=5.5 StartAngle=0 EndAngle=1.5708
    g7: ArcOfCircle CenterX=63.5 CenterY=5.5 CenterZ=0 NormalX=0 NormalY=0 NormalZ=1 AngleXU=0 Radius=5.5 StartAngle=4.71239 EndAngle=6.28319
    g8: ArcOfCircle CenterX=5.50002 CenterY=54.5 CenterZ=0 NormalX=0 NormalY=0 NormalZ=1 AngleXU=0 Radius=5.5 StartAngle=1.5708 EndAngle=3.14159
    g9: Circle CenterX=63.5 CenterY=5.5 CenterZ=0 NormalX=0 NormalY=0 NormalZ=1 AngleXU=0 Radius=1.5
    g10: Circle CenterX=63.5 CenterY=54.5 CenterZ=0 NormalX=0 NormalY=0 NormalZ=1 AngleXU=0 Radius=1.5
    g11: Circle CenterX=5.50002 CenterY=54.5 CenterZ=0 NormalX=0 NormalY=0 NormalZ=1 AngleXU=0 Radius=1.5
    g12: ArcOfCircle CenterX=5.50002 CenterY=54.5 CenterZ=0 NormalX=0 NormalY=0 NormalZ=1 AngleXU=0 Radius=3 StartAngle=4.71239 EndAngle=6.28319
    g13: ArcOfCircle CenterX=63.5 CenterY=54.5 CenterZ=0 NormalX=0 NormalY=0 NormalZ=1 AngleXU=0 Radius=3 StartAngle=3.14159 EndAngle=4.71239
    g14: ArcOfCircle CenterX=63.5 CenterY=5.5 CenterZ=0 NormalX=0 NormalY=0 NormalZ=1 AngleXU=0 Radius=3 StartAngle=1.5708 EndAngle=3.14159
    g15: ArcOfCircle CenterX=5.50002 CenterY=5.5 CenterZ=0 NormalX=0 NormalY=0 NormalZ=1 AngleXU=0 Radius=3 StartAngle=0 EndAngle=1.5708
    g16: LineSegment StartX=8.50002 StartY=54.5 StartZ=0 EndX=8.50002 EndY=58.3 EndZ=0
    g17: LineSegment StartX=5.50002 StartY=51.5 StartZ=0 EndX=1.70002 EndY=51.5 EndZ=0
    g18: LineSegment StartX=1.70002 StartY=51.5 StartZ=0 EndX=1.70002 EndY=8.5 EndZ=0
    g19: LineSegment StartX=5.50002 StartY=8.5 StartZ=0 EndX=1.70002 EndY=8.5 EndZ=0
    g20: LineSegment StartX=8.50002 StartY=5.5 StartZ=0 EndX=8.50002 EndY=1.7 EndZ=0
    g21: Circle CenterX=5.50002 CenterY=5.5 CenterZ=0 NormalX=0 NormalY=0 NormalZ=1 AngleXU=0 Radius=1.5
    g22: LineSegment StartX=63.5 StartY=51.5 StartZ=0 EndX=67.3 EndY=51.5 EndZ=0
    g23: LineSegment StartX=63.5 StartY=8.5 StartZ=0 EndX=67.3 EndY=8.5 EndZ=0
    g24: LineSegment StartX=60.5 StartY=5.5 StartZ=0 EndX=60.5 EndY=1.7 EndZ=0
    g25: LineSegment StartX=60.5 StartY=58.3 StartZ=0 EndX=60.5 EndY=54.5 EndZ=0
    g26: LineSegment StartX=2.09555e-05 StartY=54.5 StartZ=0 EndX=2.09555e-05 EndY=5.5 EndZ=0
    g27: ArcOfCircle CenterX=5.50002 CenterY=5.5 CenterZ=0 NormalX=0 NormalY=0 NormalZ=1 AngleXU=0 Radius=5.5 StartAngle=3.14159 EndAngle=4.71239
    g28: LineSegment StartX=5.50002 StartY=-5.68372e-08 StartZ=0 EndX=0 EndY=0 EndZ=0
    g29: LineSegment StartX=2.09555e-05 StartY=5.5 StartZ=0 EndX=0 EndY=0 EndZ=0
  constraints (72):
    c: Horizontal(g0)
    c: Horizontal(g2)
    c: Vertical(g1)
    c: Horizontal(g3)
    c: Horizontal(g5)
    c: Vertical(g4)
    c: Coincident(g11,g8)
    c: Coincident(g12,g8)
    c: Vertical(g16)
    c: Horizontal(g17)
    c: Tangent(g12,g17) = 1.5708
    c: Tangent(g12,g16) = -1.5708
    c: Coincident(g5,g16)
    c: Coincident(g18,g17)
    c: Vertical(g18)
    c: Horizontal(g19)
    c: Vertical(g20)
    c: Coincident(g18,g19)
    c: Tangent(g15,g19) = -1.5708
    c: Tangent(g15,g20) = 1.5708
    c: Coincident(g3,g20)
    c: Distance(g0,g2) = 60
    c: Horizontal(g22)
    c: Horizontal(g23)
    c: Vertical(g24)
    c: Coincident(g3,g24)
    c: Coincident(g4,g23)
    c: Tangent(g14,g24) = -1.5708
    c: Tangent(g14,g23) = 1.5708
    c: Tangent(g13,g22) = -1.5708
    c: Coincident(g4,g22)
    c: Coincident(g25,g5)
    c: Vertical(g25)
    c: Equal(g11,g10)
    c: Equal(g10,g9)
    c: Equal(g9,g21)
    c: Equal(g13,g12)
    c: Equal(g12,g15)
    c: Equal(g15,g14)
    c: Coincident(g6,g13)
    c: Coincident(g6,g10)
    c: Tangent(g25,g13) = -1.5708
    c: Coincident(g14,g7)
    c: Coincident(g14,g9)
    c: Tangent(g2,g8) = -1.5708
    c: Tangent(g2,g6) = -1.5708
    c: Tangent(g1,g6) = -1.5708
    c: Tangent(g1,g7) = -1.5708
    c: Tangent(g0,g7) = -1.5708
    c: Equal(g16,g19)
    c: Equal(g19,g24)
    c: Equal(g24,g23)
    c: Diameter(g11) = 3
    c: Distance(g5,g2) = 1.7
    c: Radius(g12) = 3
    c: Vertical(g26)
    c: Coincident(g27,g15)
    c: Tangent(g27,g26) = -1.5708
    c: Tangent(g27,g0) = -1.5708
    c: Coincident(g28,g0)
    c: Coincident(g28,g-1)
    c: Tangent(g28,g27)
    c: Coincident(g29,g26)
    c: Coincident(g29,g28)
    c: Tangent(g29,g27)
    c: Tangent(g26,g8) = -1.5708
    c: Equal(g8,g27)
    c: Equal(g27,g7)
    c: Equal(g7,g6)
    c: Coincident(g21,g15)
    c: Distance(g8,g1) = 69
    c: Distance(g8,g26) = 5.5
FEATURE [Part::Extrusion] Extrude004
  Base = -> Sketch004
  Dir = (0,0,1)
  DirMode = 2
  FaceMakerClass = Part::FaceMakerBullseye
  LengthFwd = 10
  LengthRev = 0
  Solid = true
  Symmetric = false
FEATURE [Part::Cut] Cut003
  Base = -> Cut002
  Tool = -> Extrude004
FEATURE [Part::Part2DObjectPython] ShapeString  # Draft 2D object (typed FeaturePython)
  FontFile = <path>
  MakeFace = true
  Placement = pos=(40.08,-36.69,0) rot=(0,0,1;1.5708rad)
  Size = 5
  String = M B − + mt32-pi
  Tracking = 0
FEATURE [Sketcher::SketchObject] Sketch006
  FullyConstrained = false
  MapMode = 5
  Placement = pos=(0,0,7) rot=(0,0,1;0rad)
  Support = -> [Cut003]
  sketch-geometry (195):
    g0: LineSegment StartX=39.2686 StartY=18.8407 StartZ=0 EndX=32.7246 EndY=18.8407 EndZ=0
    g1: LineSegment StartX=39.2686 StartY=20.0582 StartZ=0 EndX=39.2686 EndY=18.8407 EndZ=0
    g2: LineSegment StartX=34.1174 StartY=20.0678 StartZ=0 EndX=39.2686 EndY=20.0582 EndZ=0
    g3: LineSegment StartX=39.2686 StartY=21.3408 StartZ=0 EndX=34.1174 EndY=20.0678 EndZ=0
    g4: LineSegment StartX=39.2686 StartY=22.6187 StartZ=0 EndX=39.2686 EndY=21.3408 EndZ=0
    g5: LineSegment StartX=34.1174 StartY=23.9105 StartZ=0 EndX=39.2686 EndY=22.6187 EndZ=0
    g6: LineSegment StartX=39.2686 StartY=23.92 StartZ=0 EndX=34.1174 EndY=23.9105 EndZ=0
    g7: LineSegment StartX=39.2686 StartY=25.1375 StartZ=0 EndX=39.2686 EndY=23.92 EndZ=0
    g8: LineSegment StartX=32.7246 StartY=25.1375 StartZ=0 EndX=39.2686 EndY=25.1375 EndZ=0
    g9: LineSegment StartX=32.7246 StartY=23.1561 StartZ=0 EndX=32.7246 EndY=25.1375 EndZ=0
    g10: LineSegment StartX=37.1885 StartY=21.9891 StartZ=0 EndX=32.7246 EndY=23.1561 EndZ=0
    g11: LineSegment StartX=32.7246 StartY=20.8189 StartZ=0 EndX=37.1885 EndY=21.9891 EndZ=0
    g12: LineSegment StartX=32.7246 StartY=18.8407 StartZ=0 EndX=32.7246 EndY=20.8189 EndZ=0
    g13: LineSegment StartX=32.7013 StartY=27.7442 StartZ=0 EndX=32.7013 EndY=30.3575 EndZ=0
    g14: LineSegment StartX=39.2453 StartY=27.7442 StartZ=0 EndX=32.7013 EndY=27.7442 EndZ=0
    g15: LineSegment StartX=39.2453 StartY=29.9705 StartZ=0 EndX=39.2453 EndY=27.7442 EndZ=0
    g16: BSplineCurve PolesCount=3 KnotsCount=2 Degree=2 IsPeriodic=0
    g17: BSplineCurve PolesCount=3 KnotsCount=2 Degree=2 IsPeriodic=0
    g18: BSplineCurve PolesCount=3 KnotsCount=2 Degree=2 IsPeriodic=0
    g19: BSplineCurve PolesCount=3 KnotsCount=2 Degree=2 IsPeriodic=0
    g20: BSplineCurve PolesCount=3 KnotsCount=2 Degree=2 IsPeriodic=0
    g21: BSplineCurve PolesCount=3 KnotsCount=2 Degree=2 IsPeriodic=0
    g22: BSplineCurve PolesCount=3 KnotsCount=2 Degree=2 IsPeriodic=0
    g23: BSplineCurve PolesCount=3 KnotsCount=2 Degree=2 IsPeriodic=0
    g24: BSplineCurve PolesCount=3 KnotsCount=2 Degree=2 IsPeriodic=0
    g25: BSplineCurve PolesCount=3 KnotsCount=2 Degree=2 IsPeriodic=0
    g26: BSplineCurve PolesCount=3 KnotsCount=2 Degree=2 IsPeriodic=0
    g27: BSplineCurve PolesCount=3 KnotsCount=2 Degree=2 IsPeriodic=0
    g28: LineSegment StartX=36.4109 StartY=29.0568 StartZ=0 EndX=38.142 EndY=29.0568 EndZ=0
    g29: LineSegment StartX=36.4109 StartY=30.1316 StartZ=0 EndX=36.4109 EndY=29.0568 EndZ=0
    g30: BSplineCurve PolesCount=3 KnotsCount=2 Degree=2 IsPeriodic=0
    g31: BSplineCurve PolesCount=3 KnotsCount=2 Degree=2 IsPeriodic=0
    g32: BSplineCurve PolesCount=3 KnotsCount=2 Degree=2 IsPeriodic=0
    g33: BSplineCurve PolesCount=3 KnotsCount=2 Degree=2 IsPeriodic=0
    g34: BSplineCurve PolesCount=3 KnotsCount=2 Degree=2 IsPeriodic=0
    g35: BSplineCurve PolesCount=3 KnotsCount=2 Degree=2 IsPeriodic=0
    g36: LineSegment StartX=38.142 StartY=29.0568 StartZ=0 EndX=38.142 EndY=30.2891 EndZ=0
    g37: LineSegment StartX=33.8047 StartY=29.0568 StartZ=0 EndX=35.3075 EndY=29.0568 EndZ=0
    g38: LineSegment StartX=33.8047 StartY=29.8145 StartZ=0 EndX=33.8047 EndY=29.0568 EndZ=0
    g39: BSplineCurve PolesCount=3 KnotsCount=2 Degree=2 IsPeriodic=0
    g40: BSplineCurve PolesCount=3 KnotsCount=2 Degree=2 IsPeriodic=0
    g41: BSplineCurve PolesCount=3 KnotsCount=2 Degree=2 IsPeriodic=0
    g42: BSplineCurve PolesCount=3 KnotsCount=2 Degree=2 IsPeriodic=0
    g43: BSplineCurve PolesCount=3 KnotsCount=2 Degree=2 IsPeriodic=0
    g44: BSplineCurve PolesCount=3 KnotsCount=2 Degree=2 IsPeriodic=0
    g45: LineSegment StartX=35.3075 StartY=29.0568 StartZ=0 EndX=35.3075 EndY=29.9215 EndZ=0
    g46: LineSegment StartX=36.6431 StartY=36.6514 StartZ=0 EndX=35.4826 EndY=36.6514 EndZ=0
    g47: LineSegment StartX=36.6431 StartY=41.217 StartZ=0 EndX=36.6431 EndY=36.6514 EndZ=0
    g48: LineSegment StartX=35.4826 StartY=41.217 StartZ=0 EndX=36.6431 EndY=41.217 EndZ=0
    g49: LineSegment StartX=35.4826 StartY=36.6514 StartZ=0 EndX=35.4826 EndY=41.217 EndZ=0
    g50: LineSegment StartX=38.3364 StartY=46.9076 StartZ=0 EndX=36.6434 EndY=46.9076 EndZ=0
    g51: LineSegment StartX=38.3364 StartY=48.068 StartZ=0 EndX=38.3364 EndY=46.9076 EndZ=0
    g52: LineSegment StartX=36.6434 StartY=48.068 StartZ=0 EndX=38.3364 EndY=48.068 EndZ=0
    g53: LineSegment StartX=36.6434 StartY=49.7611 StartZ=0 EndX=36.6434 EndY=48.068 EndZ=0
    g54: LineSegment StartX=35.4829 StartY=49.7611 StartZ=0 EndX=36.6434 EndY=49.7611 EndZ=0
    g55: LineSegment StartX=35.4829 StartY=48.068 StartZ=0 EndX=35.4829 EndY=49.7611 EndZ=0
    g56: LineSegment StartX=33.7899 StartY=48.068 StartZ=0 EndX=35.4829 EndY=48.068 EndZ=0
    g57: LineSegment StartX=33.7899 StartY=46.9076 StartZ=0 EndX=33.7899 EndY=48.068 EndZ=0
    g58: LineSegment StartX=35.4829 StartY=46.9076 StartZ=0 EndX=33.7899 EndY=46.9076 EndZ=0
    g59: LineSegment StartX=35.4829 StartY=45.2145 StartZ=0 EndX=35.4829 EndY=46.9076 EndZ=0
    g60: LineSegment StartX=36.6434 StartY=45.2145 StartZ=0 EndX=35.4829 EndY=45.2145 EndZ=0
    g61: LineSegment StartX=36.6434 StartY=46.9076 StartZ=0 EndX=36.6434 EndY=45.2145 EndZ=0
    g62: LineSegment StartX=55.0745 StartY=15.6394 StartZ=0 EndX=55.0745 EndY=16.4682 EndZ=0
    g63: LineSegment StartX=58.458 StartY=15.6394 StartZ=0 EndX=55.0745 EndY=15.6394 EndZ=0
    g64: LineSegment StartX=58.458 StartY=16.5362 StartZ=0 EndX=58.458 EndY=15.6394 EndZ=0
    g65: LineSegment StartX=56.8076 StartY=16.5362 StartZ=0 EndX=58.458 EndY=16.5362 EndZ=0
    g66: BSplineCurve PolesCount=3 KnotsCount=2 Degree=2 IsPeriodic=0
    g67: BSplineCurve PolesCount=3 KnotsCount=2 Degree=2 IsPeriodic=0
    g68: BSplineCurve PolesCount=3 KnotsCount=2 Degree=2 IsPeriodic=0
    g69: BSplineCurve PolesCount=3 KnotsCount=2 Degree=2 IsPeriodic=0
    g70: BSplineCurve PolesCount=3 KnotsCount=2 Degree=2 IsPeriodic=0
    g71: BSplineCurve PolesCount=3 KnotsCount=2 Degree=2 IsPeriodic=0
    g72: LineSegment StartX=58.458 StartY=17.6912 StartZ=0 EndX=56.5966 EndY=17.6912 EndZ=0
    g73: LineSegment StartX=58.458 StartY=18.588 StartZ=0 EndX=58.458 EndY=17.6912 EndZ=0
    g74: LineSegment StartX=56.827 StartY=18.588 StartZ=0 EndX=58.458 EndY=18.588 EndZ=0
    g75: BSplineCurve PolesCount=3 KnotsCount=2 Degree=2 IsPeriodic=0
    g76: BSplineCurve PolesCount=3 KnotsCount=2 Degree=2 IsPeriodic=0
    g77: BSplineCurve PolesCount=3 KnotsCount=2 Degree=2 IsPeriodic=0
    g78: BSplineCurve PolesCount=3 KnotsCount=2 Degree=2 IsPeriodic=0
    g79: BSplineCurve PolesCount=3 KnotsCount=2 Degree=2 IsPeriodic=0
    g80: LineSegment StartX=58.458 StartY=19.7294 StartZ=0 EndX=56.5168 EndY=19.7294 EndZ=0
    g81: LineSegment StartX=58.458 StartY=20.6262 StartZ=0 EndX=58.458 EndY=19.7294 EndZ=0
    g82: LineSegment StartX=56.2915 StartY=20.6262 StartZ=0 EndX=58.458 EndY=20.6262 EndZ=0
    g83: BSplineCurve PolesCount=3 KnotsCount=2 Degree=2 IsPeriodic=0
    g84: BSplineCurve PolesCount=3 KnotsCount=2 Degree=2 IsPeriodic=0
    g85: BSplineCurve PolesCount=3 KnotsCount=2 Degree=2 IsPeriodic=0
    g86: BSplineCurve PolesCount=3 KnotsCount=2 Degree=2 IsPeriodic=0
    g87: BSplineCurve PolesCount=3 KnotsCount=2 Degree=2 IsPeriodic=0
    g88: BSplineCurve PolesCount=3 KnotsCount=2 Degree=2 IsPeriodic=0
    g89: BSplineCurve PolesCount=3 KnotsCount=2 Degree=2 IsPeriodic=0
    g90: BSplineCurve PolesCount=3 KnotsCount=2 Degree=2 IsPeriodic=0
    g91: LineSegment StartX=55.0745 StartY=16.4682 StartZ=0 EndX=55.5363 EndY=16.4682 EndZ=0
    g92: LineSegment StartX=55.0745 StartY=23.0585 StartZ=0 EndX=55.7947 EndY=23.0585 EndZ=0
    g93: LineSegment StartX=55.0745 StartY=22.447 StartZ=0 EndX=55.0745 EndY=23.0585 EndZ=0
    g94: LineSegment StartX=53.8788 StartY=22.447 StartZ=0 EndX=55.0745 EndY=22.447 EndZ=0
    g95: LineSegment StartX=54.4087 StartY=21.5502 StartZ=0 EndX=53.8788 EndY=22.447 EndZ=0
    g96: LineSegment StartX=55.0745 StartY=21.5502 StartZ=0 EndX=54.4087 EndY=21.5502 EndZ=0
    g97: LineSegment StartX=55.0745 StartY=21.1426 StartZ=0 EndX=55.0745 EndY=21.5502 EndZ=0
    g98: LineSegment StartX=55.7947 StartY=21.1426 StartZ=0 EndX=55.0745 EndY=21.1426 EndZ=0
    g99: LineSegment StartX=55.7947 StartY=21.5502 StartZ=0 EndX=55.7947 EndY=21.1426 EndZ=0
    g100: LineSegment StartX=57.269 StartY=21.5502 StartZ=0 EndX=55.7947 EndY=21.5502 EndZ=0
    g101: BSplineCurve PolesCount=3 KnotsCount=2 Degree=2 IsPeriodic=0
    g102: BSplineCurve PolesCount=3 KnotsCount=2 Degree=2 IsPeriodic=0
    g103: BSplineCurve PolesCount=3 KnotsCount=2 Degree=2 IsPeriodic=0
    g104: BSplineCurve PolesCount=3 KnotsCount=2 Degree=2 IsPeriodic=0
    g105: BSplineCurve PolesCount=3 KnotsCount=2 Degree=2 IsPeriodic=0
    g106: LineSegment StartX=57.7062 StartY=23.0653 StartZ=0 EndX=58.4047 EndY=23.1264 EndZ=0
    g107: BSplineCurve PolesCount=3 KnotsCount=2 Degree=2 IsPeriodic=0
    g108: BSplineCurve PolesCount=3 KnotsCount=2 Degree=2 IsPeriodic=0
    g109: BSplineCurve PolesCount=3 KnotsCount=2 Degree=2 IsPeriodic=0
    g110: BSplineCurve PolesCount=3 KnotsCount=2 Degree=2 IsPeriodic=0
    g111: LineSegment StartX=55.7947 StartY=22.447 StartZ=0 EndX=57.1539 EndY=22.447 EndZ=0
    g112: LineSegment StartX=55.7947 StartY=23.0585 StartZ=0 EndX=55.7947 EndY=22.447 EndZ=0
    g113: LineSegment StartX=57.2174 StartY=23.4525 StartZ=0 EndX=57.1127 EndY=24.3222 EndZ=0
    g114: BSplineCurve PolesCount=3 KnotsCount=2 Degree=2 IsPeriodic=0
    g115: BSplineCurve PolesCount=3 KnotsCount=2 Degree=2 IsPeriodic=0
    g116: BSplineCurve PolesCount=3 KnotsCount=2 Degree=2 IsPeriodic=0
    g117: BSplineCurve PolesCount=3 KnotsCount=2 Degree=2 IsPeriodic=0
    g118: BSplineCurve PolesCount=3 KnotsCount=2 Degree=2 IsPeriodic=0
    g119: BSplineCurve PolesCount=3 KnotsCount=2 Degree=2 IsPeriodic=0
    g120: BSplineCurve PolesCount=3 KnotsCount=2 Degree=2 IsPeriodic=0
    g121: BSplineCurve PolesCount=3 KnotsCount=2 Degree=2 IsPeriodic=0
    g122: BSplineCurve PolesCount=3 KnotsCount=2 Degree=2 IsPeriodic=0
    g123: BSplineCurve PolesCount=3 KnotsCount=2 Degree=2 IsPeriodic=0
    g124: BSplineCurve PolesCount=3 KnotsCount=2 Degree=2 IsPeriodic=0
    g125: BSplineCurve PolesCount=3 KnotsCount=2 Degree=2 IsPeriodic=0
    g126: LineSegment StartX=55.1289 StartY=24.3493 StartZ=0 EndX=54.9885 EndY=23.5205 EndZ=0
    g127: BSplineCurve PolesCount=3 KnotsCount=2 Degree=2 IsPeriodic=0
    g128: BSplineCurve PolesCount=3 KnotsCount=2 Degree=2 IsPeriodic=0
    g129: BSplineCurve PolesCount=3 KnotsCount=2 Degree=2 IsPeriodic=0
    g130: BSplineCurve PolesCount=3 KnotsCount=2 Degree=2 IsPeriodic=0
    g131: BSplineCurve PolesCount=3 KnotsCount=2 Degree=2 IsPeriodic=0
    g132: BSplineCurve PolesCount=3 KnotsCount=2 Degree=2 IsPeriodic=0
    g133: LineSegment StartX=56.3372 StartY=24.6075 StartZ=0 EndX=55.6181 EndY=24.706 EndZ=0
    g134: BSplineCurve PolesCount=3 KnotsCount=2 Degree=2 IsPeriodic=0
    g135: BSplineCurve PolesCount=3 KnotsCount=2 Degree=2 IsPeriodic=0
    g136: BSplineCurve PolesCount=3 KnotsCount=2 Degree=2 IsPeriodic=0
    g137: BSplineCurve PolesCount=3 KnotsCount=2 Degree=2 IsPeriodic=0
    g138: BSplineCurve PolesCount=3 KnotsCount=2 Degree=2 IsPeriodic=0
    g139: BSplineCurve PolesCount=3 KnotsCount=2 Degree=2 IsPeriodic=0
    g140: BSplineCurve PolesCount=3 KnotsCount=2 Degree=2 IsPeriodic=0
    g141: LineSegment StartX=57.6291 StartY=30.1515 StartZ=0 EndX=58.458 EndY=30.1515 EndZ=0
    g142: LineSegment StartX=57.6291 StartY=28.3521 StartZ=0 EndX=57.6291 EndY=30.1515 EndZ=0
    g143: BSplineCurve PolesCount=3 KnotsCount=2 Degree=2 IsPeriodic=0
    g144: BSplineCurve PolesCount=3 KnotsCount=2 Degree=2 IsPeriodic=0
    g145: BSplineCurve PolesCount=3 KnotsCount=2 Degree=2 IsPeriodic=0
    g146: BSplineCurve PolesCount=3 KnotsCount=2 Degree=2 IsPeriodic=0
    g147: BSplineCurve PolesCount=3 KnotsCount=2 Degree=2 IsPeriodic=0
    g148: BSplineCurve PolesCount=3 KnotsCount=2 Degree=2 IsPeriodic=0
    g149: BSplineCurve PolesCount=3 KnotsCount=2 Degree=2 IsPeriodic=0
    g150: BSplineCurve PolesCount=3 KnotsCount=2 Degree=2 IsPeriodic=0
    g151: BSplineCurve PolesCount=3 KnotsCount=2 Degree=2 IsPeriodic=0
    g152: LineSegment StartX=55.2376 StartY=27.991 StartZ=0 EndX=55.1478 EndY=27.0941 EndZ=0
    g153: BSplineCurve PolesCount=3 KnotsCount=2 Degree=2 IsPeriodic=0
    g154: BSplineCurve PolesCount=3 KnotsCount=2 Degree=2 IsPeriodic=0
    g155: BSplineCurve PolesCount=3 KnotsCount=2 Degree=2 IsPeriodic=0
    g156: BSplineCurve PolesCount=3 KnotsCount=2 Degree=2 IsPeriodic=0
    g157: BSplineCurve PolesCount=3 KnotsCount=2 Degree=2 IsPeriodic=0
    g158: BSplineCurve PolesCount=3 KnotsCount=2 Degree=2 IsPeriodic=0
    g159: BSplineCurve PolesCount=3 KnotsCount=2 Degree=2 IsPeriodic=0
    g160: BSplineCurve PolesCount=3 KnotsCount=2 Degree=2 IsPeriodic=0
    g161: LineSegment StartX=58.458 StartY=30.1515 StartZ=0 EndX=58.458 EndY=26.999 EndZ=0
    g162: LineSegment StartX=57.2079 StartY=30.8309 StartZ=0 EndX=56.311 EndY=30.8309 EndZ=0
    g163: LineSegment StartX=57.2079 StartY=32.5837 StartZ=0 EndX=57.2079 EndY=30.8309 EndZ=0
    g164: LineSegment StartX=56.311 StartY=32.5837 StartZ=0 EndX=57.2079 EndY=32.5837 EndZ=0
    g165: LineSegment StartX=56.311 StartY=30.8309 StartZ=0 EndX=56.311 EndY=32.5837 EndZ=0
    g166: LineSegment StartX=55.0745 StartY=33.0865 StartZ=0 EndX=55.0745 EndY=33.9154 EndZ=0
    g167: LineSegment StartX=59.7488 StartY=33.0865 StartZ=0 EndX=55.0745 EndY=33.0865 EndZ=0
    g168: LineSegment StartX=59.7488 StartY=33.9833 StartZ=0 EndX=59.7488 EndY=33.0865 EndZ=0
    g169: LineSegment StartX=58.0459 StartY=33.9833 StartZ=0 EndX=59.7488 EndY=33.9833 EndZ=0
    g170: BSplineCurve PolesCount=3 KnotsCount=2 Degree=2 IsPeriodic=0
    g171: BSplineCurve PolesCount=3 KnotsCount=2 Degree=2 IsPeriodic=0
    g172: BSplineCurve PolesCount=3 KnotsCount=2 Degree=2 IsPeriodic=0
    g173: BSplineCurve PolesCount=3 KnotsCount=2 Degree=2 IsPeriodic=0
    g174: BSplineCurve PolesCount=3 KnotsCount=2 Degree=2 IsPeriodic=0
    g175: BSplineCurve PolesCount=3 KnotsCount=2 Degree=2 IsPeriodic=0
    g176: BSplineCurve PolesCount=3 KnotsCount=2 Degree=2 IsPeriodic=0
    g177: BSplineCurve PolesCount=3 KnotsCount=2 Degree=2 IsPeriodic=0
    g178: LineSegment StartX=55.0745 StartY=33.9154 StartZ=0 EndX=55.5713 EndY=33.9154 EndZ=0
    g179: BSplineCurve PolesCount=3 KnotsCount=2 Degree=2 IsPeriodic=0
    g180: BSplineCurve PolesCount=3 KnotsCount=2 Degree=2 IsPeriodic=0
    g181: BSplineCurve PolesCount=3 KnotsCount=2 Degree=2 IsPeriodic=0
    g182: BSplineCurve PolesCount=3 KnotsCount=2 Degree=2 IsPeriodic=0
    g183: BSplineCurve PolesCount=3 KnotsCount=2 Degree=2 IsPeriodic=0
    g184: BSplineCurve PolesCount=3 KnotsCount=2 Degree=2 IsPeriodic=0
    g185: BSplineCurve PolesCount=3 KnotsCount=2 Degree=2 IsPeriodic=0
    g186: BSplineCurve PolesCount=3 KnotsCount=2 Degree=2 IsPeriodic=0
    g187: LineSegment StartX=58.458 StartY=37.0814 StartZ=0 EndX=55.0745 EndY=37.0814 EndZ=0
    g188: LineSegment StartX=58.458 StartY=37.9782 StartZ=0 EndX=58.458 EndY=37.0814 EndZ=0
    g189: LineSegment StartX=55.0745 StartY=37.9782 StartZ=0 EndX=58.458 EndY=37.9782 EndZ=0
    g190: LineSegment StartX=55.0745 StartY=37.0814 StartZ=0 EndX=55.0745 EndY=37.9782 EndZ=0
    g191: LineSegment StartX=54.6125 StartY=37.0814 StartZ=0 EndX=53.7837 EndY=37.0814 EndZ=0
    g192: LineSegment StartX=54.6125 StartY=37.9782 StartZ=0 EndX=54.6125 EndY=37.0814 EndZ=0
    g193: LineSegment StartX=53.7837 StartY=37.9782 StartZ=0 EndX=54.6125 EndY=37.9782 EndZ=0
    g194: LineSegment StartX=53.7837 StartY=37.0814 StartZ=0 EndX=53.7837 EndY=37.9782 EndZ=0
  constraints (263):
    c: Horizontal(g0)
    c: Coincident(g0,g1)
    c: Vertical(g1)
    c: Coincident(g1,g2)
    c: Coincident(g2,g3)
    c: Coincident(g3,g4)
    c: Vertical(g4)
    c: Coincident(g4,g5)
    c: Coincident(g5,g6)
    c: Coincident(g6,g7)
    c: Vertical(g7)
    c: Coincident(g7,g8)
    c: Coincident(g8,g9)
    c: Vertical(g9)
    c: Coincident(g9,g10)
    c: Coincident(g10,g11)
    c: Coincident(g11,g12)
    c: Vertical(g12)
    c: Coincident(g12,g0)
    c: Vertical(g13)
    c: Coincident(g13,g14)
    c: Horizontal(g14)
    c: Coincident(g14,g15)
    c: Vertical(g15)
    c: Coincident(g15,g16)
    c: Coincident(g16,g17)
    c: Coincident(g17,g18)
    c: Coincident(g18,g19)
    c: Coincident(g19,g20)
    c: Coincident(g20,g21)
    c: Coincident(g21,g22)
    c: Coincident(g22,g23)
    c: Coincident(g23,g24)
    c: Coincident(g24,g25)
    c: Coincident(g25,g26)
    c: Coincident(g26,g27)
    c: Coincident(g27,g13)
    c: Horizontal(g28)
    c: Coincident(g28,g29)
    c: Vertical(g29)
    c: Coincident(g29,g30)
    c: Coincident(g30,g31)
    c: Coincident(g31,g32)
    c: Coincident(g32,g33)
    c: Coincident(g33,g34)
    c: Coincident(g34,g35)
    c: Coincident(g35,g36)
    c: Vertical(g36)
    c: Coincident(g36,g28)
    c: Horizontal(g37)
    c: Coincident(g37,g38)
    c: Vertical(g38)
    c: Coincident(g38,g39)
    c: Coincident(g39,g40)
    c: Coincident(g40,g41)
    c: Coincident(g41,g42)
    c: Coincident(g42,g43)
    c: Coincident(g43,g44)
    c: Coincident(g44,g45)
    c: Vertical(g45)
    c: Coincident(g45,g37)
    c: Horizontal(g46)
    c: Coincident(g46,g47)
    c: Vertical(g47)
    c: Coincident(g47,g48)
    c: Horizontal(g48)
    c: Coincident(g48,g49)
    c: Coincident(g49,g46)
    c: Horizontal(g50)
    c: Coincident(g50,g51)
    c: Vertical(g51)
    c: Coincident(g51,g52)
    c: Horizontal(g52)
    c: Coincident(g52,g53)
    c: Vertical(g53)
    c: Coincident(g53,g54)
    c: Horizontal(g54)
    c: Coincident(g54,g55)
    c: Vertical(g55)
    c: Coincident(g55,g56)
    c: Horizontal(g56)
    c: Coincident(g56,g57)
    c: Vertical(g57)
    c: Coincident(g57,g58)
    c: Horizontal(g58)
    c: Coincident(g58,g59)
    c: Vertical(g59)
    c: Coincident(g59,g60)
    c: Horizontal(g60)
    c: Coincident(g60,g61)
    c: Vertical(g61)
    c: Coincident(g61,g50)
    c: Vertical(g62)
    c: Coincident(g62,g63)
    c: Horizontal(g63)
    c: Coincident(g63,g64)
    c: Vertical(g64)
    c: Coincident(g64,g65)
    c: Horizontal(g65)
    c: Coincident(g65,g66)
    c: Coincident(g66,g67)
    c: Coincident(g67,g68)
    c: Coincident(g68,g69)
    c: Coincident(g69,g70)
    c: Coincident(g70,g71)
    c: Coincident(g71,g72)
    c: Horizontal(g72)
    c: Coincident(g72,g73)
    c: Vertical(g73)
    c: Coincident(g73,g74)
    c: Horizontal(g74)
    c: Coincident(g74,g75)
    c: Coincident(g75,g76)
    c: Coincident(g76,g77)
    c: Coincident(g77,g78)
    c: Coincident(g78,g79)
    c: Coincident(g79,g80)
    c: Coincident(g80,g81)
    c: Vertical(g81)
    c: Coincident(g81,g82)
    c: Horizontal(g82)
    c: Coincident(g82,g83)
    c: Coincident(g83,g84)
    c: Coincident(g84,g85)
    c: Coincident(g85,g86)
    c: Coincident(g86,g87)
    c: Coincident(g87,g88)
    c: Coincident(g88,g89)
    c: Coincident(g89,g90)
    c: Coincident(g90,g91)
    c: Horizontal(g91)
    c: Coincident(g91,g62)
    c: Horizontal(g92)
    c: Coincident(g92,g93)
    c: Vertical(g93)
    c: Coincident(g93,g94)
    c: Horizontal(g94)
    c: Coincident(g94,g95)
    c: Coincident(g95,g96)
    c: Coincident(g96,g97)
    c: Vertical(g97)
    c: Coincident(g97,g98)
    c: Horizontal(g98)
    c: Coincident(g98,g99)
    c: Vertical(g99)
    c: Coincident(g99,g100)
    c: Horizontal(g100)
    c: Coincident(g100,g101)
    c: Coincident(g101,g102)
    c: Coincident(g102,g103)
    c: Coincident(g103,g104)
    c: Coincident(g104,g105)
    c: Coincident(g105,g106)
    c: Coincident(g106,g107)
    c: Coincident(g107,g108)
    c: Coincident(g108,g109)
    c: Coincident(g109,g110)
    c: Coincident(g110,g111)
    c: Horizontal(g111)
    c: Coincident(g111,g112)
    c: Vertical(g112)
    c: Coincident(g112,g92)
    c: Coincident(g113,g114)
    c: Coincident(g114,g115)
    c: Coincident(g115,g116)
    c: Coincident(g116,g117)
    c: Coincident(g117,g118)
    c: Coincident(g118,g119)
    c: Coincident(g119,g120)
    c: Coincident(g120,g121)
    c: Coincident(g121,g122)
    c: Coincident(g122,g123)
    c: Coincident(g123,g124)
    c: Coincident(g124,g125)
    c: Coincident(g125,g126)
    c: Coincident(g126,g127)
    c: Coincident(g127,g128)
    c: Coincident(g128,g129)
    c: Coincident(g129,g130)
    c: Coincident(g130,g131)
    c: Coincident(g131,g132)
    c: Coincident(g132,g133)
    c: Coincident(g133,g134)
    c: Coincident(g134,g135)
    c: Coincident(g135,g136)
    c: Coincident(g136,g137)
    c: Coincident(g137,g138)
    c: Coincident(g138,g139)
    c: Coincident(g139,g140)
    c: Coincident(g140,g113)
    c: Horizontal(g141)
    c: Coincident(g141,g142)
    c: Vertical(g142)
    c: Coincident(g142,g143)
    c: Coincident(g143,g144)
    c: Coincident(g144,g145)
    c: Coincident(g145,g146)
    c: Coincident(g146,g147)
    c: Coincident(g147,g148)
    c: Coincident(g148,g149)
    c: Coincident(g149,g150)
    c: Coincident(g150,g151)
    c: Coincident(g151,g152)
    c: Coincident(g152,g153)
    c: Coincident(g153,g154)
    c: Coincident(g154,g155)
    c: Coincident(g155,g156)
    c: Coincident(g156,g157)
    c: Coincident(g157,g158)
    c: Coincident(g158,g159)
    c: Coincident(g159,g160)
    c: Coincident(g160,g161)
    c: Vertical(g161)
    c: Coincident(g161,g141)
    c: Horizontal(g162)
    c: Coincident(g162,g163)
    c: Vertical(g163)
    c: Coincident(g163,g164)
    c: Horizontal(g164)
    c: Coincident(g164,g165)
    c: Vertical(g165)
    c: Coincident(g165,g162)
    c: Vertical(g166)
    c: Coincident(g166,g167)
    c: Horizontal(g167)
    c: Coincident(g167,g168)
    c: Vertical(g168)
    c: Coincident(g168,g169)
    c: Horizontal(g169)
    c: Coincident(g169,g170)
    c: Coincident(g170,g171)
    c: Coincident(g171,g172)
    c: Coincident(g172,g173)
    c: Coincident(g173,g174)
    c: Coincident(g174,g175)
    c: Coincident(g175,g176)
    c: Coincident(g176,g177)
    c: Coincident(g177,g178)
    c: Horizontal(g178)
    c: Coincident(g178,g166)
    c: Coincident(g179,g180)
    c: Coincident(g180,g181)
    c: Coincident(g181,g182)
    c: Coincident(g182,g183)
    c: Coincident(g183,g184)
    c: Coincident(g184,g185)
    c: Coincident(g185,g186)
    c: Coincident(g186,g179)
    c: Coincident(g187,g188)
    c: Vertical(g188)
    c: Coincident(g188,g189)
    c: Horizontal(g189)
    c: Coincident(g189,g190)
    c: Vertical(g190)
    c: Coincident(g190,g187)
    c: Horizontal(g191)
    c: Coincident(g191,g192)
    c: Vertical(g192)
    c: Coincident(g192,g193)
    c: Horizontal(g193)
    c: Coincident(g193,g194)
    c: Vertical(g194)
    c: Coincident(g194,g191)
FEATURE [Part::Extrusion] Extrude005
  Base = -> Sketch006
  Dir = (0,0,1)
  DirMode = 2
  FaceMakerClass = Part::FaceMakerBullseye
  LengthFwd = 0
  LengthRev = 0.5
  Solid = true
  Symmetric = false
FEATURE [Part::Cut] Cut004
  Base = -> Cut003
  Tool = -> Extrude005
FEATURE [Sketcher::SketchObject] Sketch007
  FullyConstrained = true
  MapMode = 5
  Placement = pos=(0,0,5) rot=(0,0,1;0rad)
  Support = -> [Cut]
  expr: Constraints[21] = Sketch001.Constraints[21]
  expr: Constraints[52] = Sketch001.Constraints[52]
  expr: Constraints[53] = Sketch001.Constraints[53]
  expr: Constraints[54] = Sketch001.Constraints[54]
  expr: Constraints[70] = Sketch001.Constraints[70]
  expr: Constraints[71] = Sketch001.Constraints[71]
  sketch-geometry (34):
    g0: LineSegment StartX=5.5 StartY=1.51013e-08 StartZ=0 EndX=63.5 EndY=1.51013e-08 EndZ=0
    g1: LineSegment StartX=69 StartY=5.5 StartZ=0 EndX=69 EndY=54.5 EndZ=0
    g2: LineSegment StartX=63.5 StartY=60 StartZ=0 EndX=5.5 EndY=60 EndZ=0
    g3: LineSegment StartX=8.5 StartY=1.7 StartZ=0 EndX=60.5 EndY=1.7 EndZ=0
    g4: LineSegment StartX=67.3 StartY=8.5 StartZ=0 EndX=67.3 EndY=51.5 EndZ=0
    g5: LineSegment StartX=60.5 StartY=58.3 StartZ=0 EndX=8.5 EndY=58.3 EndZ=0
    g6: ArcOfCircle CenterX=63.5 CenterY=54.5 CenterZ=0 NormalX=0 NormalY=0 NormalZ=1 AngleXU=0 Radius=5.5 StartAngle=0 EndAngle=1.5708
    g7: ArcOfCircle CenterX=63.5 CenterY=5.5 CenterZ=0 NormalX=0 NormalY=0 NormalZ=1 AngleXU=0 Radius=5.5 StartAngle=4.71239 EndAngle=6.28319
    g8: ArcOfCircle CenterX=5.5 CenterY=54.5 CenterZ=0 NormalX=0 NormalY=0 NormalZ=1 AngleXU=0 Radius=5.5 StartAngle=1.5708 EndAngle=3.14159
    g9: Circle CenterX=63.5 CenterY=5.5 CenterZ=0 NormalX=0 NormalY=0 NormalZ=1 AngleXU=0 Radius=1.5
    g10: Circle CenterX=63.5 CenterY=54.5 CenterZ=0 NormalX=0 NormalY=0 NormalZ=1 AngleXU=0 Radius=1.5
    g11: Circle CenterX=5.5 CenterY=54.5 CenterZ=0 NormalX=0 NormalY=0 NormalZ=1 AngleXU=0 Radius=1.5
    g12: ArcOfCircle CenterX=5.5 CenterY=54.5 CenterZ=0 NormalX=0 NormalY=0 NormalZ=1 AngleXU=0 Radius=3 StartAngle=4.71239 EndAngle=6.28319
    g13: ArcOfCircle CenterX=63.5 CenterY=54.5 CenterZ=0 NormalX=0 NormalY=0 NormalZ=1 AngleXU=0 Radius=3 StartAngle=3.14159 EndAngle=4.71239
    g14: ArcOfCircle CenterX=63.5 CenterY=5.5 CenterZ=0 NormalX=0 NormalY=0 NormalZ=1 AngleXU=0 Radius=3 StartAngle=1.5708 EndAngle=3.14159
    g15: ArcOfCircle CenterX=5.5 CenterY=5.5 CenterZ=0 NormalX=0 NormalY=0 NormalZ=1 AngleXU=0 Radius=3 StartAngle=1e-16 EndAngle=1.5708
    g16: LineSegment StartX=8.5 StartY=54.5 StartZ=0 EndX=8.5 EndY=58.3 EndZ=0
    g17: LineSegment StartX=5.5 StartY=51.5 StartZ=0 EndX=1.7 EndY=51.5 EndZ=0
    g18: LineSegment StartX=1.7 StartY=51.5 StartZ=0 EndX=1.7 EndY=8.5 EndZ=0
    g19: LineSegment StartX=5.5 StartY=8.5 StartZ=0 EndX=1.7 EndY=8.5 EndZ=0
    g20: LineSegment StartX=8.5 StartY=5.5 StartZ=0 EndX=8.5 EndY=1.7 EndZ=0
    g21: Circle CenterX=5.5 CenterY=5.5 CenterZ=0 NormalX=0 NormalY=0 NormalZ=1 AngleXU=0 Radius=1.5
    g22: LineSegment StartX=63.5 StartY=51.5 StartZ=0 EndX=67.3 EndY=51.5 EndZ=0
    g23: LineSegment StartX=63.5 StartY=8.5 StartZ=0 EndX=67.3 EndY=8.5 EndZ=0
    g24: LineSegment StartX=60.5 StartY=5.5 StartZ=0 EndX=60.5 EndY=1.7 EndZ=0
    g25: LineSegment StartX=60.5 StartY=58.3 StartZ=0 EndX=60.5 EndY=54.5 EndZ=0
    g26: LineSegment StartX=3.97114e-08 StartY=54.5 StartZ=0 EndX=3.97114e-08 EndY=5.5 EndZ=0
    g27: ArcOfCircle CenterX=5.5 CenterY=5.5 CenterZ=0 NormalX=0 NormalY=0 NormalZ=1 AngleXU=0 Radius=5.5 StartAngle=3.14159 EndAngle=4.71239
    g28: LineSegment StartX=5.5 StartY=1.51013e-08 StartZ=0 EndX=0 EndY=0 EndZ=0
    g29: LineSegment StartX=3.97114e-08 StartY=5.5 StartZ=0 EndX=0 EndY=0 EndZ=0
    g30: LineSegment StartX=67.3 StartY=51.5 StartZ=0 EndX=61.5157 EndY=51.5 EndZ=0
    g31: LineSegment StartX=61.5157 StartY=51.5 StartZ=0 EndX=61.5157 EndY=52.25 EndZ=0
    g32: LineSegment StartX=61.5157 StartY=52.25 StartZ=0 EndX=67.3 EndY=52.25 EndZ=0
    g33: LineSegment StartX=67.3 StartY=52.25 StartZ=0 EndX=67.3 EndY=51.5 EndZ=0
  constraints (83):
    c: Horizontal(g0)
    c: Horizontal(g2)
    c: Vertical(g1)
    c: Horizontal(g3)
    c: Horizontal(g5)
    c: Vertical(g4)
    c: Coincident(g11,g8)
    c: Coincident(g12,g8)
    c: Vertical(g16)
    c: Horizontal(g17)
    c: Tangent(g12,g17) = 1.5708
    c: Tangent(g12,g16) = -1.5708
    c: Coincident(g5,g16)
    c: Coincident(g18,g17)
    c: Vertical(g18)
    c: Horizontal(g19)
    c: Vertical(g20)
    c: Coincident(g18,g19)
    c: Tangent(g15,g19) = -1.5708
    c: Tangent(g15,g20) = 1.5708
    c: Coincident(g3,g20)
    c: Distance(g0,g2) = 60
    c: Horizontal(g22)
    c: Horizontal(g23)
    c: Vertical(g24)
    c: Coincident(g3,g24)
    c: Coincident(g4,g23)
    c: Tangent(g14,g24) = -1.5708
    c: Tangent(g14,g23) = 1.5708
    c: Tangent(g13,g22) = -1.5708
    c: Coincident(g4,g22)
    c: Coincident(g25,g5)
    c: Vertical(g25)
    c: Equal(g11,g10)
    c: Equal(g10,g9)
    c: Equal(g9,g21)
    c: Equal(g13,g12)
    c: Equal(g12,g15)
    c: Equal(g15,g14)
    c: Coincident(g6,g13)
    c: Coincident(g6,g10)
    c: Tangent(g25,g13) = -1.5708
    c: Coincident(g14,g7)
    c: Coincident(g14,g9)
    c: Tangent(g2,g8) = -1.5708
    c: Tangent(g2,g6) = -1.5708
    c: Tangent(g1,g6) = -1.5708
    c: Tangent(g1,g7) = -1.5708
    c: Tangent(g0,g7) = -1.5708
    c: Equal(g16,g19)
    c: Equal(g19,g24)
    c: Equal(g24,g23)
    c: Diameter(g11) = 3
    c: Distance(g5,g2) = 1.7
    c: Radius(g12) = 3
    c: Vertical(g26)
    c: Coincident(g27,g15)
    c: Tangent(g27,g26) = -1.5708
    c: Tangent(g27,g0) = -1.5708
    c: Coincident(g28,g0)
    c: Coincident(g28,g-1)
    c: Tangent(g28,g27)
    c: Coincident(g29,g26)
    c: Coincident(g29,g28)
    c: Tangent(g29,g27)
    c: Tangent(g26,g8) = -1.5708
    c: Equal(g8,g27)
    c: Equal(g27,g7)
    c: Equal(g7,g6)
    c: Coincident(g21,g15)
    c: Distance(g8,g1) = 69
    c: Distance(g8,g26) = 5.5
    c: Coincident(g30,g31)
    c: Coincident(g31,g32)
    c: Coincident(g32,g33)
    c: Coincident(g33,g30)
    c: Horizontal(g30)
    c: Horizontal(g32)
    c: Vertical(g31)
    c: Vertical(g33)
    c: Coincident(g30,g4)
    c: PointOnObject(g31,g13)
    c: Distance(g33) = 0.75
FEATURE [Part::Extrusion] Extrude007
  Base = -> Sketch007
  Dir = (0,0,1)
  DirMode = 2
  FaceMakerClass = Part::FaceMakerBullseye
  LengthFwd = 0
  LengthRev = 10
  Solid = true
  Symmetric = false
FEATURE [Part::Cut] Cut005
  Base = -> Cut
  Tool = -> Extrude007
FEATURE [Sketcher::SketchObject] Sketch008
  FullyConstrained = true
  MapMode = 5
  Placement = pos=(0,0,5) rot=(1,0,0;3.14159rad)
  Support = -> [Cut004]
  sketch-geometry (8):
    g0: LineSegment StartX=67.3 StartY=-19.27 StartZ=0 EndX=49 EndY=-19.27 EndZ=0
    g1: LineSegment StartX=49 StartY=-19.27 StartZ=0 EndX=49 EndY=-50.5 EndZ=0
    g2: LineSegment StartX=49 StartY=-50.5 StartZ=0 EndX=67.3 EndY=-50.5 EndZ=0
    g3: LineSegment StartX=67.3 StartY=-50.5 StartZ=0 EndX=67.3 EndY=-19.27 EndZ=0
    g4: LineSegment StartX=16 StartY=-47 StartZ=0 EndX=25.5 EndY=-47 EndZ=0
    g5: LineSegment StartX=25.5 StartY=-47 StartZ=0 EndX=25.5 EndY=-52 EndZ=0
    g6: LineSegment StartX=25.5 StartY=-52 StartZ=0 EndX=16 EndY=-52 EndZ=0
    g7: LineSegment StartX=16 StartY=-52 StartZ=0 EndX=16 EndY=-47 EndZ=0
  constraints (24):
    c: Coincident(g0,g1)
    c: Coincident(g1,g2)
    c: Coincident(g2,g3)
    c: Coincident(g3,g0)
    c: Horizontal(g0)
    c: Horizontal(g2)
    c: Vertical(g1)
    c: Vertical(g3)
    c: Coincident(g4,g5)
    c: Coincident(g5,g6)
    c: Coincident(g6,g7)
    c: Coincident(g7,g4)
    c: Horizontal(g4)
    c: Horizontal(g6)
    c: Vertical(g5)
    c: Vertical(g7)
    c: DistanceX(g-2,g0) = 67.3
    c: DistanceY(g-1,g1) = -50.5
    c: DistanceX(g-2,g0) = 49
    c: DistanceY(g-1,g0) = -19.27
    c: DistanceX(g-2,g4) = 16
    c: DistanceX(g-2,g4) = 25.5
    c: Distance(g6,g4) = 5
    c: DistanceY(g-1,g4) = -47
FEATURE [Part::Extrusion] Extrude010
  Base = -> Sketch008
  Dir = (0,0,-1)
  DirMode = 2
  FaceMakerClass = Part::FaceMakerBullseye
  LengthFwd = 0
  LengthRev = 0.5
  Solid = true
  Symmetric = false
FEATURE [Part::Cut] Cut006
  Base = -> Cut004
  Tool = -> Extrude010
FEATURE [Sketcher::SketchObject] Sketch009
  FullyConstrained = true
  MapMode = 5
  Placement = pos=(0,0,7) rot=(0,0,1;0rad)
  Support = -> [Cut006]
  expr: Constraints[21] = Sketch001.Constraints[21]
  expr: Constraints[52] = Sketch001.Constraints[52]
  expr: Constraints[53] = Sketch001.Constraints[53]
  expr: Constraints[54] = Sketch001.Constraints[54]
  expr: Constraints[70] = Sketch001.Constraints[70]
  expr: Constraints[71] = Sketch001.Constraints[71]
  sketch-geometry (34):
    g0: LineSegment StartX=5.5 StartY=-6.32288e-08 StartZ=0 EndX=63.5 EndY=-6.32288e-08 EndZ=0
    g1: LineSegment StartX=69 StartY=5.5 StartZ=0 EndX=69 EndY=54.5 EndZ=0
    g2: LineSegment StartX=63.5 StartY=60 StartZ=0 EndX=5.5 EndY=60 EndZ=0
    g3: LineSegment StartX=8.5 StartY=1.7 StartZ=0 EndX=60.5 EndY=1.7 EndZ=0
    g4: LineSegment StartX=67.3 StartY=8.5 StartZ=0 EndX=67.3 EndY=51.5 EndZ=0
    g5: LineSegment StartX=60.5 StartY=58.3 StartZ=0 EndX=8.5 EndY=58.3 EndZ=0
    g6: ArcOfCircle CenterX=63.5 CenterY=54.5 CenterZ=0 NormalX=0 NormalY=0 NormalZ=1 AngleXU=0 Radius=5.5 StartAngle=6e-16 EndAngle=1.5708
    g7: ArcOfCircle CenterX=63.5 CenterY=5.5 CenterZ=0 NormalX=0 NormalY=0 NormalZ=1 AngleXU=0 Radius=5.5 StartAngle=4.71239 EndAngle=6.28319
    g8: ArcOfCircle CenterX=5.5 CenterY=54.5 CenterZ=0 NormalX=0 NormalY=0 NormalZ=1 AngleXU=0 Radius=5.5 StartAngle=1.5708 EndAngle=3.14159
    g9: Circle CenterX=63.5 CenterY=5.5 CenterZ=0 NormalX=0 NormalY=0 NormalZ=1 AngleXU=0 Radius=1.5
    g10: Circle CenterX=63.5 CenterY=54.5 CenterZ=0 NormalX=0 NormalY=0 NormalZ=1 AngleXU=0 Radius=1.5
    g11: Circle CenterX=5.5 CenterY=54.5 CenterZ=0 NormalX=0 NormalY=0 NormalZ=1 AngleXU=0 Radius=1.5
    g12: ArcOfCircle CenterX=5.5 CenterY=54.5 CenterZ=0 NormalX=0 NormalY=0 NormalZ=1 AngleXU=0 Radius=3 StartAngle=4.71239 EndAngle=6.28319
    g13: ArcOfCircle CenterX=63.5 CenterY=54.5 CenterZ=0 NormalX=0 NormalY=0 NormalZ=1 AngleXU=0 Radius=3 StartAngle=3.14159 EndAngle=4.71239
    g14: ArcOfCircle CenterX=63.5 CenterY=5.5 CenterZ=0 NormalX=0 NormalY=0 NormalZ=1 AngleXU=0 Radius=3 StartAngle=1.5708 EndAngle=3.14159
    g15: ArcOfCircle CenterX=5.5 CenterY=5.5 CenterZ=0 NormalX=0 NormalY=0 NormalZ=1 AngleXU=0 Radius=3 StartAngle=1e-16 EndAngle=1.5708
    g16: LineSegment StartX=8.5 StartY=54.5 StartZ=0 EndX=8.5 EndY=58.3 EndZ=0
    g17: LineSegment StartX=5.5 StartY=51.5 StartZ=0 EndX=1.7 EndY=51.5 EndZ=0
    g18: LineSegment StartX=1.7 StartY=51.5 StartZ=0 EndX=1.7 EndY=8.5 EndZ=0
    g19: LineSegment StartX=5.5 StartY=8.5 StartZ=0 EndX=1.7 EndY=8.5 EndZ=0
    g20: LineSegment StartX=8.5 StartY=5.5 StartZ=0 EndX=8.5 EndY=1.7 EndZ=0
    g21: Circle CenterX=5.5 CenterY=5.5 CenterZ=0 NormalX=0 NormalY=0 NormalZ=1 AngleXU=0 Radius=1.5
    g22: LineSegment StartX=63.5 StartY=51.5 StartZ=0 EndX=67.3 EndY=51.5 EndZ=0
    g23: LineSegment StartX=63.5 StartY=8.5 StartZ=0 EndX=67.3 EndY=8.5 EndZ=0
    g24: LineSegment StartX=60.5 StartY=5.5 StartZ=0 EndX=60.5 EndY=1.7 EndZ=0
    g25: LineSegment StartX=60.5 StartY=58.3 StartZ=0 EndX=60.5 EndY=54.5 EndZ=0
    g26: LineSegment StartX=2.63401e-06 StartY=54.5 StartZ=0 EndX=2.63401e-06 EndY=5.5 EndZ=0
    g27: ArcOfCircle CenterX=5.5 CenterY=5.5 CenterZ=0 NormalX=0 NormalY=0 NormalZ=1 AngleXU=0 Radius=5.5 StartAngle=3.14159 EndAngle=4.71239
    g28: LineSegment StartX=5.5 StartY=-6.32288e-08 StartZ=0 EndX=0 EndY=0 EndZ=0
    g29: LineSegment StartX=2.63401e-06 StartY=5.5 StartZ=0 EndX=0 EndY=0 EndZ=0
    g30: Circle CenterX=5.5 CenterY=54.5 CenterZ=0 NormalX=0 NormalY=0 NormalZ=1 AngleXU=0 Radius=2.8
    g31: Circle CenterX=5.5 CenterY=5.5 CenterZ=0 NormalX=0 NormalY=0 NormalZ=1 AngleXU=0 Radius=2.8
    g32: Circle CenterX=63.5 CenterY=5.5 CenterZ=0 NormalX=0 NormalY=0 NormalZ=1 AngleXU=0 Radius=2.8
    g33: Circle CenterX=63.5 CenterY=54.5 CenterZ=0 NormalX=0 NormalY=0 NormalZ=1 AngleXU=0 Radius=2.8
  constraints (80):
    c: Horizontal(g0)
    c: Horizontal(g2)
    c: Vertical(g1)
    c: Horizontal(g3)
    c: Horizontal(g5)
    c: Vertical(g4)
    c: Coincident(g11,g8)
    c: Coincident(g12,g8)
    c: Vertical(g16)
    c: Horizontal(g17)
    c: Tangent(g12,g17) = 1.5708
    c: Tangent(g12,g16) = -1.5708
    c: Coincident(g5,g16)
    c: Coincident(g18,g17)
    c: Vertical(g18)
    c: Horizontal(g19)
    c: Vertical(g20)
    c: Coincident(g18,g19)
    c: Tangent(g15,g19) = -1.5708
    c: Tangent(g15,g20) = 1.5708
    c: Coincident(g3,g20)
    c: Distance(g0,g2) = 60
    c: Horizontal(g22)
    c: Horizontal(g23)
    c: Vertical(g24)
    c: Coincident(g3,g24)
    c: Coincident(g4,g23)
    c: Tangent(g14,g24) = -1.5708
    c: Tangent(g14,g23) = 1.5708
    c: Tangent(g13,g22) = -1.5708
    c: Coincident(g4,g22)
    c: Coincident(g25,g5)
    c: Vertical(g25)
    c: Equal(g11,g10)
    c: Equal(g10,g9)
    c: Equal(g9,g21)
    c: Equal(g13,g12)
    c: Equal(g12,g15)
    c: Equal(g15,g14)
    c: Coincident(g6,g13)
    c: Coincident(g6,g10)
    c: Tangent(g25,g13) = -1.5708
    c: Coincident(g14,g7)
    c: Coincident(g14,g9)
    c: Tangent(g2,g8) = -1.5708
    c: Tangent(g2,g6) = -1.5708
    c: Tangent(g1,g6) = -1.5708
    c: Tangent(g1,g7) = -1.5708
    c: Tangent(g0,g7) = -1.5708
    c: Equal(g16,g19)
    c: Equal(g19,g24)
    c: Equal(g24,g23)
    c: Diameter(g11) = 3
    c: Distance(g5,g2) = 1.7
    c: Radius(g12) = 3
    c: Vertical(g26)
    c: Coincident(g27,g15)
    c: Tangent(g27,g26) = -1.5708
    c: Tangent(g27,g0) = -1.5708
    c: Coincident(g28,g0)
    c: Coincident(g28,g-1)
    c: Tangent(g28,g27)
    c: Coincident(g29,g26)
    c: Coincident(g29,g28)
    c: Tangent(g29,g27)
    c: Tangent(g26,g8) = -1.5708
    c: Equal(g8,g27)
    c: Equal(g27,g7)
    c: Equal(g7,g6)
    c: Coincident(g21,g15)
    c: Distance(g8,g1) = 69
    c: Distance(g8,g26) = 5.5
    c: Coincident(g30,g8)
    c: Coincident(g31,g15)
    c: Coincident(g32,g7)
    c: Coincident(g33,g6)
    c: Equal(g33,g30)
    c: Equal(g30,g31)
    c: Equal(g31,g32)
    c: Diameter(g30) = 5.6
FEATURE [Part::Extrusion] Extrude011
  Base = -> Sketch009
  Dir = (0,0,1)
  DirMode = 2
  FaceMakerClass = Part::FaceMakerBullseye
  LengthFwd = 0
  LengthRev = 1
  Solid = true
  Symmetric = false
FEATURE [Part::Cut] Cut007
  Base = -> Cut006
  Tool = -> Extrude011
FEATURE [Part::Chamfer] Chamfer
  Base = -> Cut007
  Edges = 20 edges r=1: [Edge107,Edge108,Edge109,Edge110,Edge211,Edge212,Edge213,Edge214,Edge231,Edge232,Edge233,Edge234,Edge239,Edge240,Edge241,Edge242,Edge280,Edge281,Edge282,Edge283]
FEATURE [Part::MultiFuse] Fusion
  Shapes = -> [Cut001,Cut005,Chamfer]
FEATURE [Mesh::Feature] Mesh  label="Fusion (Meshed)"
  Placement = pos=(0,-11,1.3e-15) rot=(1,0,0;3.14159rad)
note: 1 file-system path scrubbed to <path> (originals preserved in the JSON sidecar)
